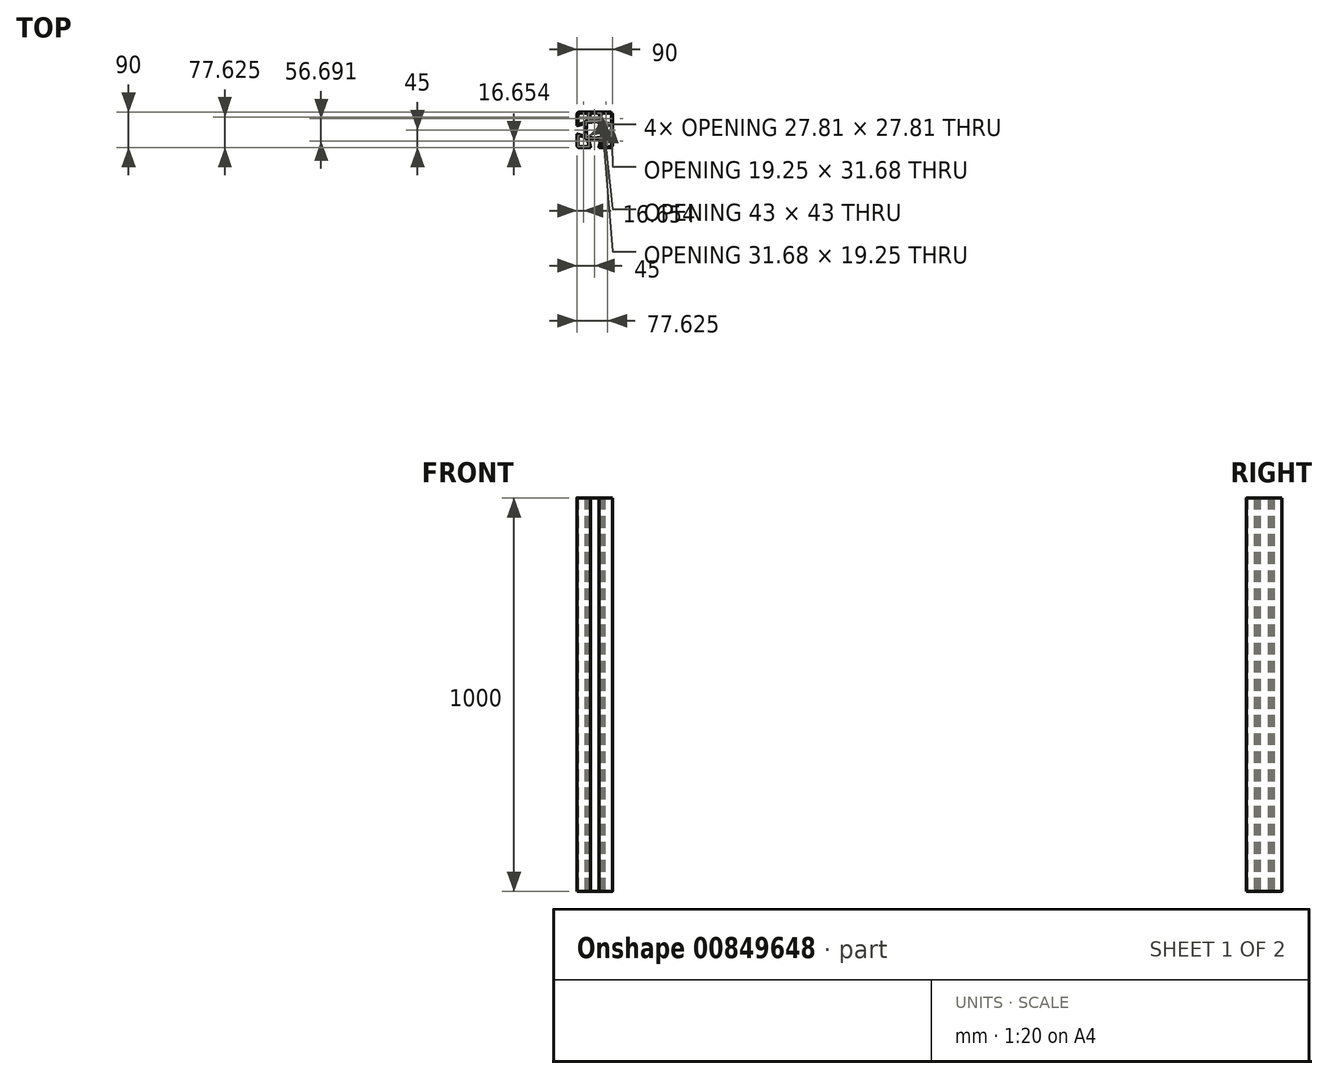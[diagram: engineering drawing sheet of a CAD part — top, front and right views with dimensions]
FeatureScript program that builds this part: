
annotation { "Feature Type Name" : "Feature", "Feature Type Description" : "" }
export const myFeature = defineFeature(function(context is Context, id is Id, definition is map)
    precondition{}
    {
        {
            var Q0;
            Q0=qCreatedBy(makeId("Top.planeOp"),FACE);
            var sketch = newSketch(context, id + "F0", { "sketchPlane" : qUnion([Q0])});
            skLineSegment(sketch, "E0", {"start": v(24.26, -15.8) * mm, "end": v(42.25, -10.99) * mm});
            skLineSegment(sketch, "E1", {"start": v(42.25, -10.99) * mm, "end": v(42.25, 10.99) * mm});
            skLineSegment(sketch, "E2", {"start": v(42.25, 10.99) * mm, "end": v(24.26, 15.8) * mm});
            skLineSegment(sketch, "E3", {"start": v(23, 14.84) * mm, "end": v(23, 9.27) * mm});
            skLineSegment(sketch, "E4", {"start": v(23, -9.27) * mm, "end": v(23, -14.84) * mm});
            skLineSegment(sketch, "E5", {"start": v(24.48, 18.6) * mm, "end": v(39.73, 14.5) * mm});
            skLineSegment(sketch, "E6", {"start": v(42.25, 16.44) * mm, "end": v(42.25, 39) * mm});
            skLineSegment(sketch, "E7", {"start": v(39, 42.25) * mm, "end": v(16.44, 42.25) * mm});
            skLineSegment(sketch, "E8", {"start": v(14.5, 39.73) * mm, "end": v(18.6, 24.48) * mm});
            skLineSegment(sketch, "E9", {"start": v(20.53, 23) * mm, "end": v(21, 23) * mm});
            skLineSegment(sketch, "E10", {"start": v(23, 21) * mm, "end": v(23, 20.53) * mm});
            skLineSegment(sketch, "E11", {"start": v(-18.6, 24.48) * mm, "end": v(-14.5, 39.73) * mm});
            skLineSegment(sketch, "E12", {"start": v(-16.44, 42.25) * mm, "end": v(-39, 42.25) * mm});
            skLineSegment(sketch, "E13", {"start": v(-42.25, 39) * mm, "end": v(-42.25, 16.44) * mm});
            skLineSegment(sketch, "E14", {"start": v(-39.73, 14.5) * mm, "end": v(-24.48, 18.6) * mm});
            skLineSegment(sketch, "E15", {"start": v(-23, 20.53) * mm, "end": v(-23, 21) * mm});
            skLineSegment(sketch, "E16", {"start": v(-21, 23) * mm, "end": v(-20.53, 23) * mm});
            skLineSegment(sketch, "E17", {"start": v(-19.25, -20.25) * mm, "end": v(-7.4, -20.25) * mm});
            skLineSegment(sketch, "E18", {"start": v(7.4, -20.25) * mm, "end": v(19.25, -20.25) * mm});
            skLineSegment(sketch, "E19", {"start": v(20.25, -19.25) * mm, "end": v(20.25, -7.4) * mm});
            skLineSegment(sketch, "E20", {"start": v(20.25, 7.4) * mm, "end": v(20.25, 19.25) * mm});
            skLineSegment(sketch, "E21", {"start": v(19.25, 20.25) * mm, "end": v(7.4, 20.25) * mm});
            skLineSegment(sketch, "E22", {"start": v(-7.4, 20.25) * mm, "end": v(-19.25, 20.25) * mm});
            skLineSegment(sketch, "E23", {"start": v(-20.25, 19.25) * mm, "end": v(-20.25, 7.4) * mm});
            skLineSegment(sketch, "E24", {"start": v(-20.25, -7.4) * mm, "end": v(-20.25, -19.25) * mm});
            skLineSegment(sketch, "E25", {"start": v(9.27, -23) * mm, "end": v(14.84, -23) * mm});
            skLineSegment(sketch, "E26", {"start": v(-14.84, -23) * mm, "end": v(-9.27, -23) * mm});
            skLineSegment(sketch, "E27", {"start": v(-10.67, -43.43) * mm, "end": v(-15.8, -24.26) * mm});
            skLineSegment(sketch, "E28", {"start": v(-39, -45) * mm, "end": v(-11.88, -45) * mm});
            skLineSegment(sketch, "E29", {"start": v(-45, -11.88) * mm, "end": v(-45, -39) * mm});
            skLineSegment(sketch, "E30", {"start": v(-24.26, -15.8) * mm, "end": v(-43.43, -10.67) * mm});
            skLineSegment(sketch, "E31", {"start": v(-23, -9.27) * mm, "end": v(-23, -14.84) * mm});
            skLineSegment(sketch, "E32", {"start": v(-23, 14.84) * mm, "end": v(-23, 9.27) * mm});
            skLineSegment(sketch, "E33", {"start": v(-43.43, 10.67) * mm, "end": v(-24.26, 15.8) * mm});
            skLineSegment(sketch, "E34", {"start": v(-45, 39) * mm, "end": v(-45, 11.88) * mm});
            skLineSegment(sketch, "E35", {"start": v(39, 45) * mm, "end": v(-39, 45) * mm});
            skLineSegment(sketch, "E36", {"start": v(45, -39) * mm, "end": v(45, 39) * mm});
            skLineSegment(sketch, "E37", {"start": v(11.88, -45) * mm, "end": v(39, -45) * mm});
            skLineSegment(sketch, "E38", {"start": v(15.8, -24.26) * mm, "end": v(10.67, -43.43) * mm});
            skLineSegment(sketch, "E39", {"start": v(-14.84, 23) * mm, "end": v(-9.27, 23) * mm});
            skLineSegment(sketch, "E40", {"start": v(9.27, 23) * mm, "end": v(14.84, 23) * mm});
            skLineSegment(sketch, "E41", {"start": v(15.8, 24.26) * mm, "end": v(10.99, 42.25) * mm});
            skLineSegment(sketch, "E42", {"start": v(10.99, 42.25) * mm, "end": v(-10.99, 42.25) * mm});
            skLineSegment(sketch, "E43", {"start": v(-10.99, 42.25) * mm, "end": v(-15.8, 24.26) * mm});
            skLineSegment(sketch, "E44", {"start": v(-24.48, -18.6) * mm, "end": v(-39.73, -14.5) * mm});
            skLineSegment(sketch, "E45", {"start": v(-42.25, -16.44) * mm, "end": v(-42.25, -39) * mm});
            skLineSegment(sketch, "E46", {"start": v(-39, -42.25) * mm, "end": v(-16.44, -42.25) * mm});
            skLineSegment(sketch, "E47", {"start": v(-14.5, -39.73) * mm, "end": v(-18.6, -24.48) * mm});
            skLineSegment(sketch, "E48", {"start": v(-20.53, -23) * mm, "end": v(-21, -23) * mm});
            skLineSegment(sketch, "E49", {"start": v(-23, -21) * mm, "end": v(-23, -20.53) * mm});
            skLineSegment(sketch, "E50", {"start": v(18.6, -24.48) * mm, "end": v(14.5, -39.73) * mm});
            skLineSegment(sketch, "E51", {"start": v(16.44, -42.25) * mm, "end": v(39, -42.25) * mm});
            skLineSegment(sketch, "E52", {"start": v(42.25, -39) * mm, "end": v(42.25, -16.44) * mm});
            skLineSegment(sketch, "E53", {"start": v(39.73, -14.5) * mm, "end": v(24.48, -18.6) * mm});
            skLineSegment(sketch, "E54", {"start": v(23, -20.53) * mm, "end": v(23, -21) * mm});
            skLineSegment(sketch, "E55", {"start": v(21, -23) * mm, "end": v(20.53, -23) * mm});
            skArc(sketch, "E56", {"start": v(23, -14.84) * mm, "mid": v(23.4, -15.64) * mm, "end": v(24.26, -15.8) * mm});
            skArc(sketch, "E57", {"start": v(24.26, 15.8) * mm, "mid": v(23.4, 15.64) * mm, "end": v(23, 14.84) * mm});
            skArc(sketch, "E58", {"start": v(23, 9.27) * mm, "mid": v(23.02, 9.06) * mm, "end": v(23.09, 8.86) * mm});
            skArc(sketch, "E59", {"start": v(23.09, -8.86) * mm, "mid": v(25, 0) * mm, "end": v(23.09, 8.86) * mm});
            skArc(sketch, "E60", {"start": v(23.09, -8.86) * mm, "mid": v(23.02, -9.06) * mm, "end": v(23, -9.27) * mm});
            skArc(sketch, "E61", {"start": v(23, 20.53) * mm, "mid": v(23.41, 19.3) * mm, "end": v(24.48, 18.6) * mm});
            skArc(sketch, "E62", {"start": v(39.73, 14.5) * mm, "mid": v(41.47, 14.85) * mm, "end": v(42.25, 16.44) * mm});
            skArc(sketch, "E63", {"start": v(42.25, 39) * mm, "mid": v(41.3, 41.3) * mm, "end": v(39, 42.25) * mm});
            skArc(sketch, "E64", {"start": v(16.44, 42.25) * mm, "mid": v(14.85, 41.47) * mm, "end": v(14.5, 39.73) * mm});
            skArc(sketch, "E65", {"start": v(18.6, 24.48) * mm, "mid": v(19.3, 23.41) * mm, "end": v(20.53, 23) * mm});
            skArc(sketch, "E66", {"start": v(23, 21) * mm, "mid": v(22.41, 22.41) * mm, "end": v(21, 23) * mm});
            skArc(sketch, "E67", {"start": v(-20.53, 23) * mm, "mid": v(-19.3, 23.41) * mm, "end": v(-18.6, 24.48) * mm});
            skArc(sketch, "E68", {"start": v(-14.5, 39.73) * mm, "mid": v(-14.85, 41.47) * mm, "end": v(-16.44, 42.25) * mm});
            skArc(sketch, "E69", {"start": v(-39, 42.25) * mm, "mid": v(-41.3, 41.3) * mm, "end": v(-42.25, 39) * mm});
            skArc(sketch, "E70", {"start": v(-42.25, 16.44) * mm, "mid": v(-41.47, 14.85) * mm, "end": v(-39.73, 14.5) * mm});
            skArc(sketch, "E71", {"start": v(-24.48, 18.6) * mm, "mid": v(-23.41, 19.3) * mm, "end": v(-23, 20.53) * mm});
            skArc(sketch, "E72", {"start": v(-21, 23) * mm, "mid": v(-22.41, 22.41) * mm, "end": v(-23, 21) * mm});
            skArc(sketch, "E73", {"start": v(-20.25, -19.25) * mm, "mid": v(-19.96, -19.96) * mm, "end": v(-19.25, -20.25) * mm});
            skArc(sketch, "E74", {"start": v(-7.07, -20.3) * mm, "mid": v(-7.23, -20.26) * mm, "end": v(-7.4, -20.25) * mm});
            skArc(sketch, "E75", {"start": v(-7.07, -20.3) * mm, "mid": v(0, -21.5) * mm, "end": v(7.07, -20.3) * mm});
            skArc(sketch, "E76", {"start": v(7.4, -20.25) * mm, "mid": v(7.23, -20.26) * mm, "end": v(7.07, -20.3) * mm});
            skArc(sketch, "E77", {"start": v(19.25, -20.25) * mm, "mid": v(19.96, -19.96) * mm, "end": v(20.25, -19.25) * mm});
            skArc(sketch, "E78", {"start": v(20.3, -7.07) * mm, "mid": v(20.26, -7.23) * mm, "end": v(20.25, -7.4) * mm});
            skArc(sketch, "E79", {"start": v(20.3, -7.07) * mm, "mid": v(21.5, 0) * mm, "end": v(20.3, 7.07) * mm});
            skArc(sketch, "E80", {"start": v(20.25, 7.4) * mm, "mid": v(20.26, 7.23) * mm, "end": v(20.3, 7.07) * mm});
            skArc(sketch, "E81", {"start": v(20.25, 19.25) * mm, "mid": v(19.96, 19.96) * mm, "end": v(19.25, 20.25) * mm});
            skArc(sketch, "E82", {"start": v(7.07, 20.3) * mm, "mid": v(7.23, 20.26) * mm, "end": v(7.4, 20.25) * mm});
            skArc(sketch, "E83", {"start": v(7.07, 20.3) * mm, "mid": v(0, 21.5) * mm, "end": v(-7.07, 20.3) * mm});
            skArc(sketch, "E84", {"start": v(-7.4, 20.25) * mm, "mid": v(-7.23, 20.26) * mm, "end": v(-7.07, 20.3) * mm});
            skArc(sketch, "E85", {"start": v(-19.25, 20.25) * mm, "mid": v(-19.96, 19.96) * mm, "end": v(-20.25, 19.25) * mm});
            skArc(sketch, "E86", {"start": v(-20.3, 7.07) * mm, "mid": v(-20.26, 7.23) * mm, "end": v(-20.25, 7.4) * mm});
            skArc(sketch, "E87", {"start": v(-20.3, 7.07) * mm, "mid": v(-21.5, 0) * mm, "end": v(-20.3, -7.07) * mm});
            skArc(sketch, "E88", {"start": v(-20.25, -7.4) * mm, "mid": v(-20.26, -7.23) * mm, "end": v(-20.3, -7.07) * mm});
            skArc(sketch, "E89", {"start": v(15.8, -24.26) * mm, "mid": v(15.64, -23.4) * mm, "end": v(14.84, -23) * mm});
            skArc(sketch, "E90", {"start": v(9.27, -23) * mm, "mid": v(9.06, -23.02) * mm, "end": v(8.86, -23.09) * mm});
            skArc(sketch, "E91", {"start": v(-8.86, -23.09) * mm, "mid": v(0, -25) * mm, "end": v(8.86, -23.09) * mm});
            skArc(sketch, "E92", {"start": v(-8.86, -23.09) * mm, "mid": v(-9.06, -23.02) * mm, "end": v(-9.27, -23) * mm});
            skArc(sketch, "E93", {"start": v(-14.84, -23) * mm, "mid": v(-15.64, -23.4) * mm, "end": v(-15.8, -24.26) * mm});
            skArc(sketch, "E94", {"start": v(-11.88, -45) * mm, "mid": v(-10.89, -44.51) * mm, "end": v(-10.67, -43.43) * mm});
            skArc(sketch, "E95", {"start": v(-45, -39) * mm, "mid": v(-43.24, -43.24) * mm, "end": v(-39, -45) * mm});
            skArc(sketch, "E96", {"start": v(-43.43, -10.67) * mm, "mid": v(-44.51, -10.89) * mm, "end": v(-45, -11.88) * mm});
            skArc(sketch, "E97", {"start": v(-24.26, -15.8) * mm, "mid": v(-23.4, -15.64) * mm, "end": v(-23, -14.84) * mm});
            skArc(sketch, "E98", {"start": v(-23, -9.27) * mm, "mid": v(-23.02, -9.06) * mm, "end": v(-23.09, -8.86) * mm});
            skArc(sketch, "E99", {"start": v(-23.09, 8.86) * mm, "mid": v(-25, 0) * mm, "end": v(-23.09, -8.86) * mm});
            skArc(sketch, "E100", {"start": v(-23.09, 8.86) * mm, "mid": v(-23.02, 9.06) * mm, "end": v(-23, 9.27) * mm});
            skArc(sketch, "E101", {"start": v(-23, 14.84) * mm, "mid": v(-23.4, 15.64) * mm, "end": v(-24.26, 15.8) * mm});
            skArc(sketch, "E102", {"start": v(-45, 11.88) * mm, "mid": v(-44.51, 10.89) * mm, "end": v(-43.43, 10.67) * mm});
            skArc(sketch, "E103", {"start": v(-39, 45) * mm, "mid": v(-43.24, 43.24) * mm, "end": v(-45, 39) * mm});
            skArc(sketch, "E104", {"start": v(45, 39) * mm, "mid": v(43.24, 43.24) * mm, "end": v(39, 45) * mm});
            skArc(sketch, "E105", {"start": v(39, -45) * mm, "mid": v(43.24, -43.24) * mm, "end": v(45, -39) * mm});
            skArc(sketch, "E106", {"start": v(10.67, -43.43) * mm, "mid": v(10.89, -44.51) * mm, "end": v(11.88, -45) * mm});
            skArc(sketch, "E107", {"start": v(-15.8, 24.26) * mm, "mid": v(-15.64, 23.4) * mm, "end": v(-14.84, 23) * mm});
            skArc(sketch, "E108", {"start": v(-9.27, 23) * mm, "mid": v(-9.06, 23.02) * mm, "end": v(-8.86, 23.09) * mm});
            skArc(sketch, "E109", {"start": v(8.86, 23.09) * mm, "mid": v(0, 25) * mm, "end": v(-8.86, 23.09) * mm});
            skArc(sketch, "E110", {"start": v(8.86, 23.09) * mm, "mid": v(9.06, 23.02) * mm, "end": v(9.27, 23) * mm});
            skArc(sketch, "E111", {"start": v(14.84, 23) * mm, "mid": v(15.64, 23.4) * mm, "end": v(15.8, 24.26) * mm});
            skArc(sketch, "E112", {"start": v(-23, -20.53) * mm, "mid": v(-23.41, -19.3) * mm, "end": v(-24.48, -18.6) * mm});
            skArc(sketch, "E113", {"start": v(-39.73, -14.5) * mm, "mid": v(-41.47, -14.85) * mm, "end": v(-42.25, -16.44) * mm});
            skArc(sketch, "E114", {"start": v(-42.25, -39) * mm, "mid": v(-41.3, -41.3) * mm, "end": v(-39, -42.25) * mm});
            skArc(sketch, "E115", {"start": v(-16.44, -42.25) * mm, "mid": v(-14.85, -41.47) * mm, "end": v(-14.5, -39.73) * mm});
            skArc(sketch, "E116", {"start": v(-18.6, -24.48) * mm, "mid": v(-19.3, -23.41) * mm, "end": v(-20.53, -23) * mm});
            skArc(sketch, "E117", {"start": v(-23, -21) * mm, "mid": v(-22.41, -22.41) * mm, "end": v(-21, -23) * mm});
            skArc(sketch, "E118", {"start": v(20.53, -23) * mm, "mid": v(19.3, -23.41) * mm, "end": v(18.6, -24.48) * mm});
            skArc(sketch, "E119", {"start": v(14.5, -39.73) * mm, "mid": v(14.85, -41.47) * mm, "end": v(16.44, -42.25) * mm});
            skArc(sketch, "E120", {"start": v(39, -42.25) * mm, "mid": v(41.3, -41.3) * mm, "end": v(42.25, -39) * mm});
            skArc(sketch, "E121", {"start": v(42.25, -16.44) * mm, "mid": v(41.47, -14.85) * mm, "end": v(39.73, -14.5) * mm});
            skArc(sketch, "E122", {"start": v(24.48, -18.6) * mm, "mid": v(23.41, -19.3) * mm, "end": v(23, -20.53) * mm});
            skArc(sketch, "E123", {"start": v(21, -23) * mm, "mid": v(22.41, -22.41) * mm, "end": v(23, -21) * mm});
            skLineSegment(sketch, "E124.1.0.0", {"start": v(57.75, 39) * mm, "end": v(57.75, 16.44) * mm});
            skLineSegment(sketch, "E124.1.0.1", {"start": v(115.8, 24.26) * mm, "end": v(110.99, 42.25) * mm});
            skLineSegment(sketch, "E124.1.0.2", {"start": v(89.01, 42.25) * mm, "end": v(84.2, 24.26) * mm});
            skArc(sketch, "E124.1.0.3", {"start": v(107.07, 20.3) * mm, "mid": v(100, 21.5) * mm, "end": v(92.93, 20.3) * mm});
            skLineSegment(sketch, "E124.1.0.4", {"start": v(60.27, 14.5) * mm, "end": v(75.52, 18.6) * mm});
            skLineSegment(sketch, "E124.1.0.5", {"start": v(81.4, 24.48) * mm, "end": v(85.5, 39.73) * mm});
            skLineSegment(sketch, "E124.1.0.6", {"start": v(139, 45) * mm, "end": v(61, 45) * mm});
            skArc(sketch, "E124.1.0.7", {"start": v(139, -45) * mm, "mid": v(143.24, -43.24) * mm, "end": v(145, -39) * mm});
            skArc(sketch, "E124.1.0.8", {"start": v(92.93, -20.3) * mm, "mid": v(100, -21.5) * mm, "end": v(107.07, -20.3) * mm});
            skLineSegment(sketch, "E124.1.0.9", {"start": v(120.25, -19.25) * mm, "end": v(120.25, -7.4) * mm});
            skLineSegment(sketch, "E124.1.0.10", {"start": v(79.75, 19.25) * mm, "end": v(79.75, 7.4) * mm});
            skLineSegment(sketch, "E124.1.0.11", {"start": v(118.6, -24.48) * mm, "end": v(114.5, -39.73) * mm});
            skArc(sketch, "E124.1.0.12", {"start": v(76.91, 8.86) * mm, "mid": v(75, 0) * mm, "end": v(76.91, -8.86) * mm});
            skLineSegment(sketch, "E124.1.0.13", {"start": v(114.5, 39.73) * mm, "end": v(118.6, 24.48) * mm});
            skLineSegment(sketch, "E124.1.0.14", {"start": v(116.44, -42.25) * mm, "end": v(139, -42.25) * mm});
            skLineSegment(sketch, "E124.1.0.15", {"start": v(110.99, 42.25) * mm, "end": v(89.01, 42.25) * mm});
            skLineSegment(sketch, "E124.1.0.16", {"start": v(55, 39) * mm, "end": v(55, 11.88) * mm});
            skLineSegment(sketch, "E124.1.0.17", {"start": v(120.25, 7.4) * mm, "end": v(120.25, 19.25) * mm});
            skLineSegment(sketch, "E124.1.0.18", {"start": v(55, -11.88) * mm, "end": v(55, -39) * mm});
            skLineSegment(sketch, "E124.1.0.19", {"start": v(142.25, -39) * mm, "end": v(142.25, -16.44) * mm});
            skLineSegment(sketch, "E124.1.0.20", {"start": v(57.75, -16.44) * mm, "end": v(57.75, -39) * mm});
            skArc(sketch, "E124.1.0.21", {"start": v(61, 45) * mm, "mid": v(56.76, 43.24) * mm, "end": v(55, 39) * mm});
            skArc(sketch, "E124.1.0.22", {"start": v(123.09, -8.86) * mm, "mid": v(125, 0) * mm, "end": v(123.09, 8.86) * mm});
            skArc(sketch, "E124.1.0.23", {"start": v(108.86, 23.09) * mm, "mid": v(100, 25) * mm, "end": v(91.14, 23.09) * mm});
            skLineSegment(sketch, "E124.1.0.24", {"start": v(142.25, 16.44) * mm, "end": v(142.25, 39) * mm});
            skArc(sketch, "E124.1.0.25", {"start": v(55, -39) * mm, "mid": v(56.76, -43.24) * mm, "end": v(61, -45) * mm});
            skArc(sketch, "E124.1.0.26", {"start": v(120.3, -7.07) * mm, "mid": v(121.5, 0) * mm, "end": v(120.3, 7.07) * mm});
            skLineSegment(sketch, "E124.1.0.27", {"start": v(142.25, -10.99) * mm, "end": v(142.25, 10.99) * mm});
            skLineSegment(sketch, "E124.1.0.28", {"start": v(139.73, -14.5) * mm, "end": v(124.48, -18.6) * mm});
            skLineSegment(sketch, "E124.1.0.29", {"start": v(79.75, -7.4) * mm, "end": v(79.75, -19.25) * mm});
            skLineSegment(sketch, "E124.1.0.30", {"start": v(124.48, 18.6) * mm, "end": v(139.73, 14.5) * mm});
            skLineSegment(sketch, "E124.1.0.31", {"start": v(75.74, -15.8) * mm, "end": v(56.57, -10.67) * mm});
            skLineSegment(sketch, "E124.1.0.32", {"start": v(139, 42.25) * mm, "end": v(116.44, 42.25) * mm});
            skLineSegment(sketch, "E124.1.0.33", {"start": v(124.26, -15.8) * mm, "end": v(142.25, -10.99) * mm});
            skLineSegment(sketch, "E124.1.0.34", {"start": v(89.33, -43.43) * mm, "end": v(84.2, -24.26) * mm});
            skLineSegment(sketch, "E124.1.0.35", {"start": v(75.52, -18.6) * mm, "end": v(60.27, -14.5) * mm});
            skLineSegment(sketch, "E124.1.0.36", {"start": v(61, -42.25) * mm, "end": v(83.56, -42.25) * mm});
            skLineSegment(sketch, "E124.1.0.37", {"start": v(115.8, -24.26) * mm, "end": v(110.67, -43.43) * mm});
            skLineSegment(sketch, "E124.1.0.38", {"start": v(61, -45) * mm, "end": v(88.12, -45) * mm});
            skLineSegment(sketch, "E124.1.0.39", {"start": v(142.25, 10.99) * mm, "end": v(124.26, 15.8) * mm});
            skArc(sketch, "E124.1.0.40", {"start": v(79.7, 7.07) * mm, "mid": v(78.5, 0) * mm, "end": v(79.7, -7.07) * mm});
            skLineSegment(sketch, "E124.1.0.41", {"start": v(85.5, -39.73) * mm, "end": v(81.4, -24.48) * mm});
            skLineSegment(sketch, "E124.1.0.42", {"start": v(56.57, 10.67) * mm, "end": v(75.74, 15.8) * mm});
            skArc(sketch, "E124.1.0.43", {"start": v(145, 39) * mm, "mid": v(143.24, 43.24) * mm, "end": v(139, 45) * mm});
            skArc(sketch, "E124.1.0.44", {"start": v(91.14, -23.09) * mm, "mid": v(100, -25) * mm, "end": v(108.86, -23.09) * mm});
            skLineSegment(sketch, "E124.1.0.45", {"start": v(83.56, 42.25) * mm, "end": v(61, 42.25) * mm});
            skLineSegment(sketch, "E124.1.0.46", {"start": v(111.88, -45) * mm, "end": v(139, -45) * mm});
            skLineSegment(sketch, "E124.1.0.47", {"start": v(145, -39) * mm, "end": v(145, 39) * mm});
            skLineSegment(sketch, "E124.1.0.48", {"start": v(77, 14.84) * mm, "end": v(77, 9.27) * mm});
            skArc(sketch, "E124.1.0.49", {"start": v(57.75, 16.44) * mm, "mid": v(58.53, 14.85) * mm, "end": v(60.27, 14.5) * mm});
            skLineSegment(sketch, "E124.1.0.50", {"start": v(119.25, 20.25) * mm, "end": v(107.4, 20.25) * mm});
            skArc(sketch, "E124.1.0.51", {"start": v(114.84, 23) * mm, "mid": v(115.64, 23.4) * mm, "end": v(115.8, 24.26) * mm});
            skArc(sketch, "E124.1.0.52", {"start": v(84.2, 24.26) * mm, "mid": v(84.36, 23.4) * mm, "end": v(85.16, 23) * mm});
            skArc(sketch, "E124.1.0.53", {"start": v(56.57, -10.67) * mm, "mid": v(55.49, -10.89) * mm, "end": v(55, -11.88) * mm});
            skArc(sketch, "E124.1.0.54", {"start": v(77, 14.84) * mm, "mid": v(76.6, 15.64) * mm, "end": v(75.74, 15.8) * mm});
            skArc(sketch, "E124.1.0.55", {"start": v(85.5, 39.73) * mm, "mid": v(85.15, 41.47) * mm, "end": v(83.56, 42.25) * mm});
            skArc(sketch, "E124.1.0.56", {"start": v(139, -42.25) * mm, "mid": v(141.3, -41.3) * mm, "end": v(142.25, -39) * mm});
            skLineSegment(sketch, "E124.1.0.57", {"start": v(107.4, -20.25) * mm, "end": v(119.25, -20.25) * mm});
            skArc(sketch, "E124.1.0.58", {"start": v(61, 42.25) * mm, "mid": v(58.7, 41.3) * mm, "end": v(57.75, 39) * mm});
            skArc(sketch, "E124.1.0.59", {"start": v(83.56, -42.25) * mm, "mid": v(85.15, -41.47) * mm, "end": v(85.5, -39.73) * mm});
            skLineSegment(sketch, "E124.1.0.60", {"start": v(80.75, -20.25) * mm, "end": v(92.6, -20.25) * mm});
            skArc(sketch, "E124.1.0.61", {"start": v(123, -14.84) * mm, "mid": v(123.4, -15.64) * mm, "end": v(124.26, -15.8) * mm});
            skArc(sketch, "E124.1.0.62", {"start": v(142.25, -16.44) * mm, "mid": v(141.47, -14.85) * mm, "end": v(139.73, -14.5) * mm});
            skLineSegment(sketch, "E124.1.0.63", {"start": v(123, 14.84) * mm, "end": v(123, 9.27) * mm});
            skArc(sketch, "E124.1.0.64", {"start": v(60.27, -14.5) * mm, "mid": v(58.53, -14.85) * mm, "end": v(57.75, -16.44) * mm});
            skArc(sketch, "E124.1.0.65", {"start": v(116.44, 42.25) * mm, "mid": v(114.85, 41.47) * mm, "end": v(114.5, 39.73) * mm});
            skArc(sketch, "E124.1.0.66", {"start": v(110.67, -43.43) * mm, "mid": v(110.89, -44.51) * mm, "end": v(111.88, -45) * mm});
            skArc(sketch, "E124.1.0.67", {"start": v(118.6, 24.48) * mm, "mid": v(119.3, 23.41) * mm, "end": v(120.53, 23) * mm});
            skLineSegment(sketch, "E124.1.0.68", {"start": v(77, -9.27) * mm, "end": v(77, -14.84) * mm});
            skArc(sketch, "E124.1.0.69", {"start": v(75.74, -15.8) * mm, "mid": v(76.6, -15.64) * mm, "end": v(77, -14.84) * mm});
            skLineSegment(sketch, "E124.1.0.70", {"start": v(123, -9.27) * mm, "end": v(123, -14.84) * mm});
            skLineSegment(sketch, "E124.1.0.71", {"start": v(109.27, 23) * mm, "end": v(114.84, 23) * mm});
            skArc(sketch, "E124.1.0.72", {"start": v(55, 11.88) * mm, "mid": v(55.49, 10.89) * mm, "end": v(56.57, 10.67) * mm});
            skArc(sketch, "E124.1.0.73", {"start": v(139.73, 14.5) * mm, "mid": v(141.47, 14.85) * mm, "end": v(142.25, 16.44) * mm});
            skLineSegment(sketch, "E124.1.0.74", {"start": v(92.6, 20.25) * mm, "end": v(80.75, 20.25) * mm});
            skArc(sketch, "E124.1.0.75", {"start": v(114.5, -39.73) * mm, "mid": v(114.85, -41.47) * mm, "end": v(116.44, -42.25) * mm});
            skLineSegment(sketch, "E124.1.0.76", {"start": v(109.27, -23) * mm, "end": v(114.84, -23) * mm});
            skLineSegment(sketch, "E124.1.0.77", {"start": v(85.16, 23) * mm, "end": v(90.73, 23) * mm});
            skArc(sketch, "E124.1.0.78", {"start": v(120.25, 19.25) * mm, "mid": v(119.96, 19.96) * mm, "end": v(119.25, 20.25) * mm});
            skArc(sketch, "E124.1.0.79", {"start": v(142.25, 39) * mm, "mid": v(141.3, 41.3) * mm, "end": v(139, 42.25) * mm});
            skArc(sketch, "E124.1.0.80", {"start": v(120.53, -23) * mm, "mid": v(119.3, -23.41) * mm, "end": v(118.6, -24.48) * mm});
            skArc(sketch, "E124.1.0.81", {"start": v(79.47, 23) * mm, "mid": v(80.7, 23.41) * mm, "end": v(81.4, 24.48) * mm});
            skArc(sketch, "E124.1.0.82", {"start": v(115.8, -24.26) * mm, "mid": v(115.64, -23.4) * mm, "end": v(114.84, -23) * mm});
            skArc(sketch, "E124.1.0.83", {"start": v(85.16, -23) * mm, "mid": v(84.36, -23.4) * mm, "end": v(84.2, -24.26) * mm});
            skArc(sketch, "E124.1.0.84", {"start": v(119.25, -20.25) * mm, "mid": v(119.96, -19.96) * mm, "end": v(120.25, -19.25) * mm});
            skArc(sketch, "E124.1.0.85", {"start": v(79.75, -19.25) * mm, "mid": v(80.04, -19.96) * mm, "end": v(80.75, -20.25) * mm});
            skArc(sketch, "E124.1.0.86", {"start": v(80.75, 20.25) * mm, "mid": v(80.04, 19.96) * mm, "end": v(79.75, 19.25) * mm});
            skArc(sketch, "E124.1.0.87", {"start": v(88.12, -45) * mm, "mid": v(89.11, -44.51) * mm, "end": v(89.33, -43.43) * mm});
            skLineSegment(sketch, "E124.1.0.88", {"start": v(85.16, -23) * mm, "end": v(90.73, -23) * mm});
            skArc(sketch, "E124.1.0.89", {"start": v(81.4, -24.48) * mm, "mid": v(80.7, -23.41) * mm, "end": v(79.47, -23) * mm});
            skArc(sketch, "E124.1.0.90", {"start": v(57.75, -39) * mm, "mid": v(58.7, -41.3) * mm, "end": v(61, -42.25) * mm});
            skArc(sketch, "E124.1.0.91", {"start": v(124.26, 15.8) * mm, "mid": v(123.4, 15.64) * mm, "end": v(123, 14.84) * mm});
            skArc(sketch, "E124.1.0.92", {"start": v(123.09, -8.86) * mm, "mid": v(123.02, -9.06) * mm, "end": v(123, -9.27) * mm});
            skArc(sketch, "E124.1.0.93", {"start": v(77, -20.53) * mm, "mid": v(76.59, -19.3) * mm, "end": v(75.52, -18.6) * mm});
            skArc(sketch, "E124.1.0.94", {"start": v(77, -21) * mm, "mid": v(77.59, -22.41) * mm, "end": v(79, -23) * mm});
            skLineSegment(sketch, "E124.1.0.95", {"start": v(79, 23) * mm, "end": v(79.47, 23) * mm});
            skArc(sketch, "E124.1.0.96", {"start": v(108.86, 23.09) * mm, "mid": v(109.06, 23.02) * mm, "end": v(109.27, 23) * mm});
            skArc(sketch, "E124.1.0.97", {"start": v(123, 9.27) * mm, "mid": v(123.02, 9.06) * mm, "end": v(123.09, 8.86) * mm});
            skArc(sketch, "E124.1.0.98", {"start": v(120.25, 7.4) * mm, "mid": v(120.26, 7.23) * mm, "end": v(120.3, 7.07) * mm});
            skArc(sketch, "E124.1.0.99", {"start": v(79, 23) * mm, "mid": v(77.59, 22.41) * mm, "end": v(77, 21) * mm});
            skArc(sketch, "E124.1.0.100", {"start": v(79.75, -7.4) * mm, "mid": v(79.74, -7.23) * mm, "end": v(79.7, -7.07) * mm});
            skArc(sketch, "E124.1.0.101", {"start": v(76.91, 8.86) * mm, "mid": v(76.98, 9.06) * mm, "end": v(77, 9.27) * mm});
            skArc(sketch, "E124.1.0.102", {"start": v(92.6, 20.25) * mm, "mid": v(92.77, 20.26) * mm, "end": v(92.93, 20.3) * mm});
            skLineSegment(sketch, "E124.1.0.103", {"start": v(79.47, -23) * mm, "end": v(79, -23) * mm});
            skArc(sketch, "E124.1.0.104", {"start": v(120.3, -7.07) * mm, "mid": v(120.26, -7.23) * mm, "end": v(120.25, -7.4) * mm});
            skArc(sketch, "E124.1.0.105", {"start": v(79.7, 7.07) * mm, "mid": v(79.74, 7.23) * mm, "end": v(79.75, 7.4) * mm});
            skArc(sketch, "E124.1.0.106", {"start": v(90.73, 23) * mm, "mid": v(90.94, 23.02) * mm, "end": v(91.14, 23.09) * mm});
            skLineSegment(sketch, "E124.1.0.107", {"start": v(77, -21) * mm, "end": v(77, -20.53) * mm});
            skArc(sketch, "E124.1.0.108", {"start": v(75.52, 18.6) * mm, "mid": v(76.59, 19.3) * mm, "end": v(77, 20.53) * mm});
            skArc(sketch, "E124.1.0.109", {"start": v(77, -9.27) * mm, "mid": v(76.98, -9.06) * mm, "end": v(76.91, -8.86) * mm});
            skArc(sketch, "E124.1.0.110", {"start": v(107.07, 20.3) * mm, "mid": v(107.23, 20.26) * mm, "end": v(107.4, 20.25) * mm});
            skLineSegment(sketch, "E124.1.0.111", {"start": v(120.53, 23) * mm, "end": v(121, 23) * mm});
            skArc(sketch, "E124.1.0.112", {"start": v(124.48, -18.6) * mm, "mid": v(123.41, -19.3) * mm, "end": v(123, -20.53) * mm});
            skArc(sketch, "E124.1.0.113", {"start": v(107.4, -20.25) * mm, "mid": v(107.23, -20.26) * mm, "end": v(107.07, -20.3) * mm});
            skArc(sketch, "E124.1.0.114", {"start": v(121, -23) * mm, "mid": v(122.41, -22.41) * mm, "end": v(123, -21) * mm});
            skLineSegment(sketch, "E124.1.0.115", {"start": v(121, -23) * mm, "end": v(120.53, -23) * mm});
            skLineSegment(sketch, "E124.1.0.116", {"start": v(123, -20.53) * mm, "end": v(123, -21) * mm});
            skArc(sketch, "E124.1.0.117", {"start": v(109.27, -23) * mm, "mid": v(109.06, -23.02) * mm, "end": v(108.86, -23.09) * mm});
            skArc(sketch, "E124.1.0.118", {"start": v(91.14, -23.09) * mm, "mid": v(90.94, -23.02) * mm, "end": v(90.73, -23) * mm});
            skArc(sketch, "E124.1.0.119", {"start": v(123, 20.53) * mm, "mid": v(123.41, 19.3) * mm, "end": v(124.48, 18.6) * mm});
            skArc(sketch, "E124.1.0.120", {"start": v(92.93, -20.3) * mm, "mid": v(92.77, -20.26) * mm, "end": v(92.6, -20.25) * mm});
            skLineSegment(sketch, "E124.1.0.121", {"start": v(77, 20.53) * mm, "end": v(77, 21) * mm});
            skArc(sketch, "E124.1.0.122", {"start": v(123, 21) * mm, "mid": v(122.41, 22.41) * mm, "end": v(121, 23) * mm});
            skLineSegment(sketch, "E124.1.0.123", {"start": v(123, 21) * mm, "end": v(123, 20.53) * mm});
            skLineSegment(sketch, "E124.2.0.0", {"start": v(157.75, 39) * mm, "end": v(157.75, 16.44) * mm});
            skLineSegment(sketch, "E124.2.0.1", {"start": v(215.8, 24.26) * mm, "end": v(210.99, 42.25) * mm});
            skLineSegment(sketch, "E124.2.0.2", {"start": v(189.01, 42.25) * mm, "end": v(184.2, 24.26) * mm});
            skArc(sketch, "E124.2.0.3", {"start": v(207.07, 20.3) * mm, "mid": v(200, 21.5) * mm, "end": v(192.93, 20.3) * mm});
            skLineSegment(sketch, "E124.2.0.4", {"start": v(160.27, 14.5) * mm, "end": v(175.52, 18.6) * mm});
            skLineSegment(sketch, "E124.2.0.5", {"start": v(181.4, 24.48) * mm, "end": v(185.5, 39.73) * mm});
            skLineSegment(sketch, "E124.2.0.6", {"start": v(239, 45) * mm, "end": v(161, 45) * mm});
            skArc(sketch, "E124.2.0.7", {"start": v(239, -45) * mm, "mid": v(243.24, -43.24) * mm, "end": v(245, -39) * mm});
            skArc(sketch, "E124.2.0.8", {"start": v(192.93, -20.3) * mm, "mid": v(200, -21.5) * mm, "end": v(207.07, -20.3) * mm});
            skLineSegment(sketch, "E124.2.0.9", {"start": v(220.25, -19.25) * mm, "end": v(220.25, -7.4) * mm});
            skLineSegment(sketch, "E124.2.0.10", {"start": v(179.75, 19.25) * mm, "end": v(179.75, 7.4) * mm});
            skLineSegment(sketch, "E124.2.0.11", {"start": v(218.6, -24.48) * mm, "end": v(214.5, -39.73) * mm});
            skArc(sketch, "E124.2.0.12", {"start": v(176.91, 8.86) * mm, "mid": v(175, 0) * mm, "end": v(176.91, -8.86) * mm});
            skLineSegment(sketch, "E124.2.0.13", {"start": v(214.5, 39.73) * mm, "end": v(218.6, 24.48) * mm});
            skLineSegment(sketch, "E124.2.0.14", {"start": v(216.44, -42.25) * mm, "end": v(239, -42.25) * mm});
            skLineSegment(sketch, "E124.2.0.15", {"start": v(210.99, 42.25) * mm, "end": v(189.01, 42.25) * mm});
            skLineSegment(sketch, "E124.2.0.16", {"start": v(155, 39) * mm, "end": v(155, 11.88) * mm});
            skLineSegment(sketch, "E124.2.0.17", {"start": v(220.25, 7.4) * mm, "end": v(220.25, 19.25) * mm});
            skLineSegment(sketch, "E124.2.0.18", {"start": v(155, -11.88) * mm, "end": v(155, -39) * mm});
            skLineSegment(sketch, "E124.2.0.19", {"start": v(242.25, -39) * mm, "end": v(242.25, -16.44) * mm});
            skLineSegment(sketch, "E124.2.0.20", {"start": v(157.75, -16.44) * mm, "end": v(157.75, -39) * mm});
            skArc(sketch, "E124.2.0.21", {"start": v(161, 45) * mm, "mid": v(156.76, 43.24) * mm, "end": v(155, 39) * mm});
            skArc(sketch, "E124.2.0.22", {"start": v(223.09, -8.86) * mm, "mid": v(225, 0) * mm, "end": v(223.09, 8.86) * mm});
            skArc(sketch, "E124.2.0.23", {"start": v(208.86, 23.09) * mm, "mid": v(200, 25) * mm, "end": v(191.14, 23.09) * mm});
            skLineSegment(sketch, "E124.2.0.24", {"start": v(242.25, 16.44) * mm, "end": v(242.25, 39) * mm});
            skArc(sketch, "E124.2.0.25", {"start": v(155, -39) * mm, "mid": v(156.76, -43.24) * mm, "end": v(161, -45) * mm});
            skArc(sketch, "E124.2.0.26", {"start": v(220.3, -7.07) * mm, "mid": v(221.5, 0) * mm, "end": v(220.3, 7.07) * mm});
            skLineSegment(sketch, "E124.2.0.27", {"start": v(242.25, -10.99) * mm, "end": v(242.25, 10.99) * mm});
            skLineSegment(sketch, "E124.2.0.28", {"start": v(239.73, -14.5) * mm, "end": v(224.48, -18.6) * mm});
            skLineSegment(sketch, "E124.2.0.29", {"start": v(179.75, -7.4) * mm, "end": v(179.75, -19.25) * mm});
            skLineSegment(sketch, "E124.2.0.30", {"start": v(224.48, 18.6) * mm, "end": v(239.73, 14.5) * mm});
            skLineSegment(sketch, "E124.2.0.31", {"start": v(175.74, -15.8) * mm, "end": v(156.57, -10.67) * mm});
            skLineSegment(sketch, "E124.2.0.32", {"start": v(239, 42.25) * mm, "end": v(216.44, 42.25) * mm});
            skLineSegment(sketch, "E124.2.0.33", {"start": v(224.26, -15.8) * mm, "end": v(242.25, -10.99) * mm});
            skLineSegment(sketch, "E124.2.0.34", {"start": v(189.33, -43.43) * mm, "end": v(184.2, -24.26) * mm});
            skLineSegment(sketch, "E124.2.0.35", {"start": v(175.52, -18.6) * mm, "end": v(160.27, -14.5) * mm});
            skLineSegment(sketch, "E124.2.0.36", {"start": v(161, -42.25) * mm, "end": v(183.56, -42.25) * mm});
            skLineSegment(sketch, "E124.2.0.37", {"start": v(215.8, -24.26) * mm, "end": v(210.67, -43.43) * mm});
            skLineSegment(sketch, "E124.2.0.38", {"start": v(161, -45) * mm, "end": v(188.12, -45) * mm});
            skLineSegment(sketch, "E124.2.0.39", {"start": v(242.25, 10.99) * mm, "end": v(224.26, 15.8) * mm});
            skArc(sketch, "E124.2.0.40", {"start": v(179.7, 7.07) * mm, "mid": v(178.5, 0) * mm, "end": v(179.7, -7.07) * mm});
            skLineSegment(sketch, "E124.2.0.41", {"start": v(185.5, -39.73) * mm, "end": v(181.4, -24.48) * mm});
            skLineSegment(sketch, "E124.2.0.42", {"start": v(156.57, 10.67) * mm, "end": v(175.74, 15.8) * mm});
            skArc(sketch, "E124.2.0.43", {"start": v(245, 39) * mm, "mid": v(243.24, 43.24) * mm, "end": v(239, 45) * mm});
            skArc(sketch, "E124.2.0.44", {"start": v(191.14, -23.09) * mm, "mid": v(200, -25) * mm, "end": v(208.86, -23.09) * mm});
            skLineSegment(sketch, "E124.2.0.45", {"start": v(183.56, 42.25) * mm, "end": v(161, 42.25) * mm});
            skLineSegment(sketch, "E124.2.0.46", {"start": v(211.88, -45) * mm, "end": v(239, -45) * mm});
            skLineSegment(sketch, "E124.2.0.47", {"start": v(245, -39) * mm, "end": v(245, 39) * mm});
            skLineSegment(sketch, "E124.2.0.48", {"start": v(177, 14.84) * mm, "end": v(177, 9.27) * mm});
            skArc(sketch, "E124.2.0.49", {"start": v(157.75, 16.44) * mm, "mid": v(158.53, 14.85) * mm, "end": v(160.27, 14.5) * mm});
            skLineSegment(sketch, "E124.2.0.50", {"start": v(219.25, 20.25) * mm, "end": v(207.4, 20.25) * mm});
            skArc(sketch, "E124.2.0.51", {"start": v(214.84, 23) * mm, "mid": v(215.64, 23.4) * mm, "end": v(215.8, 24.26) * mm});
            skArc(sketch, "E124.2.0.52", {"start": v(184.2, 24.26) * mm, "mid": v(184.36, 23.4) * mm, "end": v(185.16, 23) * mm});
            skArc(sketch, "E124.2.0.53", {"start": v(156.57, -10.67) * mm, "mid": v(155.49, -10.89) * mm, "end": v(155, -11.88) * mm});
            skArc(sketch, "E124.2.0.54", {"start": v(177, 14.84) * mm, "mid": v(176.6, 15.64) * mm, "end": v(175.74, 15.8) * mm});
            skArc(sketch, "E124.2.0.55", {"start": v(185.5, 39.73) * mm, "mid": v(185.15, 41.47) * mm, "end": v(183.56, 42.25) * mm});
            skArc(sketch, "E124.2.0.56", {"start": v(239, -42.25) * mm, "mid": v(241.3, -41.3) * mm, "end": v(242.25, -39) * mm});
            skLineSegment(sketch, "E124.2.0.57", {"start": v(207.4, -20.25) * mm, "end": v(219.25, -20.25) * mm});
            skArc(sketch, "E124.2.0.58", {"start": v(161, 42.25) * mm, "mid": v(158.7, 41.3) * mm, "end": v(157.75, 39) * mm});
            skArc(sketch, "E124.2.0.59", {"start": v(183.56, -42.25) * mm, "mid": v(185.15, -41.47) * mm, "end": v(185.5, -39.73) * mm});
            skLineSegment(sketch, "E124.2.0.60", {"start": v(180.75, -20.25) * mm, "end": v(192.6, -20.25) * mm});
            skArc(sketch, "E124.2.0.61", {"start": v(223, -14.84) * mm, "mid": v(223.4, -15.64) * mm, "end": v(224.26, -15.8) * mm});
            skArc(sketch, "E124.2.0.62", {"start": v(242.25, -16.44) * mm, "mid": v(241.47, -14.85) * mm, "end": v(239.73, -14.5) * mm});
            skLineSegment(sketch, "E124.2.0.63", {"start": v(223, 14.84) * mm, "end": v(223, 9.27) * mm});
            skArc(sketch, "E124.2.0.64", {"start": v(160.27, -14.5) * mm, "mid": v(158.53, -14.85) * mm, "end": v(157.75, -16.44) * mm});
            skArc(sketch, "E124.2.0.65", {"start": v(216.44, 42.25) * mm, "mid": v(214.85, 41.47) * mm, "end": v(214.5, 39.73) * mm});
            skArc(sketch, "E124.2.0.66", {"start": v(210.67, -43.43) * mm, "mid": v(210.89, -44.51) * mm, "end": v(211.88, -45) * mm});
            skArc(sketch, "E124.2.0.67", {"start": v(218.6, 24.48) * mm, "mid": v(219.3, 23.41) * mm, "end": v(220.53, 23) * mm});
            skLineSegment(sketch, "E124.2.0.68", {"start": v(177, -9.27) * mm, "end": v(177, -14.84) * mm});
            skArc(sketch, "E124.2.0.69", {"start": v(175.74, -15.8) * mm, "mid": v(176.6, -15.64) * mm, "end": v(177, -14.84) * mm});
            skLineSegment(sketch, "E124.2.0.70", {"start": v(223, -9.27) * mm, "end": v(223, -14.84) * mm});
            skLineSegment(sketch, "E124.2.0.71", {"start": v(209.27, 23) * mm, "end": v(214.84, 23) * mm});
            skArc(sketch, "E124.2.0.72", {"start": v(155, 11.88) * mm, "mid": v(155.49, 10.89) * mm, "end": v(156.57, 10.67) * mm});
            skArc(sketch, "E124.2.0.73", {"start": v(239.73, 14.5) * mm, "mid": v(241.47, 14.85) * mm, "end": v(242.25, 16.44) * mm});
            skLineSegment(sketch, "E124.2.0.74", {"start": v(192.6, 20.25) * mm, "end": v(180.75, 20.25) * mm});
            skArc(sketch, "E124.2.0.75", {"start": v(214.5, -39.73) * mm, "mid": v(214.85, -41.47) * mm, "end": v(216.44, -42.25) * mm});
            skLineSegment(sketch, "E124.2.0.76", {"start": v(209.27, -23) * mm, "end": v(214.84, -23) * mm});
            skLineSegment(sketch, "E124.2.0.77", {"start": v(185.16, 23) * mm, "end": v(190.73, 23) * mm});
            skArc(sketch, "E124.2.0.78", {"start": v(220.25, 19.25) * mm, "mid": v(219.96, 19.96) * mm, "end": v(219.25, 20.25) * mm});
            skArc(sketch, "E124.2.0.79", {"start": v(242.25, 39) * mm, "mid": v(241.3, 41.3) * mm, "end": v(239, 42.25) * mm});
            skArc(sketch, "E124.2.0.80", {"start": v(220.53, -23) * mm, "mid": v(219.3, -23.41) * mm, "end": v(218.6, -24.48) * mm});
            skArc(sketch, "E124.2.0.81", {"start": v(179.47, 23) * mm, "mid": v(180.7, 23.41) * mm, "end": v(181.4, 24.48) * mm});
            skArc(sketch, "E124.2.0.82", {"start": v(215.8, -24.26) * mm, "mid": v(215.64, -23.4) * mm, "end": v(214.84, -23) * mm});
            skArc(sketch, "E124.2.0.83", {"start": v(185.16, -23) * mm, "mid": v(184.36, -23.4) * mm, "end": v(184.2, -24.26) * mm});
            skArc(sketch, "E124.2.0.84", {"start": v(219.25, -20.25) * mm, "mid": v(219.96, -19.96) * mm, "end": v(220.25, -19.25) * mm});
            skArc(sketch, "E124.2.0.85", {"start": v(179.75, -19.25) * mm, "mid": v(180.04, -19.96) * mm, "end": v(180.75, -20.25) * mm});
            skArc(sketch, "E124.2.0.86", {"start": v(180.75, 20.25) * mm, "mid": v(180.04, 19.96) * mm, "end": v(179.75, 19.25) * mm});
            skArc(sketch, "E124.2.0.87", {"start": v(188.12, -45) * mm, "mid": v(189.11, -44.51) * mm, "end": v(189.33, -43.43) * mm});
            skLineSegment(sketch, "E124.2.0.88", {"start": v(185.16, -23) * mm, "end": v(190.73, -23) * mm});
            skArc(sketch, "E124.2.0.89", {"start": v(181.4, -24.48) * mm, "mid": v(180.7, -23.41) * mm, "end": v(179.47, -23) * mm});
            skArc(sketch, "E124.2.0.90", {"start": v(157.75, -39) * mm, "mid": v(158.7, -41.3) * mm, "end": v(161, -42.25) * mm});
            skArc(sketch, "E124.2.0.91", {"start": v(224.26, 15.8) * mm, "mid": v(223.4, 15.64) * mm, "end": v(223, 14.84) * mm});
            skArc(sketch, "E124.2.0.92", {"start": v(223.09, -8.86) * mm, "mid": v(223.02, -9.06) * mm, "end": v(223, -9.27) * mm});
            skArc(sketch, "E124.2.0.93", {"start": v(177, -20.53) * mm, "mid": v(176.59, -19.3) * mm, "end": v(175.52, -18.6) * mm});
            skArc(sketch, "E124.2.0.94", {"start": v(177, -21) * mm, "mid": v(177.59, -22.41) * mm, "end": v(179, -23) * mm});
            skLineSegment(sketch, "E124.2.0.95", {"start": v(179, 23) * mm, "end": v(179.47, 23) * mm});
            skArc(sketch, "E124.2.0.96", {"start": v(208.86, 23.09) * mm, "mid": v(209.06, 23.02) * mm, "end": v(209.27, 23) * mm});
            skArc(sketch, "E124.2.0.97", {"start": v(223, 9.27) * mm, "mid": v(223.02, 9.06) * mm, "end": v(223.09, 8.86) * mm});
            skArc(sketch, "E124.2.0.98", {"start": v(220.25, 7.4) * mm, "mid": v(220.26, 7.23) * mm, "end": v(220.3, 7.07) * mm});
            skArc(sketch, "E124.2.0.99", {"start": v(179, 23) * mm, "mid": v(177.59, 22.41) * mm, "end": v(177, 21) * mm});
            skArc(sketch, "E124.2.0.100", {"start": v(179.75, -7.4) * mm, "mid": v(179.74, -7.23) * mm, "end": v(179.7, -7.07) * mm});
            skArc(sketch, "E124.2.0.101", {"start": v(176.91, 8.86) * mm, "mid": v(176.98, 9.06) * mm, "end": v(177, 9.27) * mm});
            skArc(sketch, "E124.2.0.102", {"start": v(192.6, 20.25) * mm, "mid": v(192.77, 20.26) * mm, "end": v(192.93, 20.3) * mm});
            skLineSegment(sketch, "E124.2.0.103", {"start": v(179.47, -23) * mm, "end": v(179, -23) * mm});
            skArc(sketch, "E124.2.0.104", {"start": v(220.3, -7.07) * mm, "mid": v(220.26, -7.23) * mm, "end": v(220.25, -7.4) * mm});
            skArc(sketch, "E124.2.0.105", {"start": v(179.7, 7.07) * mm, "mid": v(179.74, 7.23) * mm, "end": v(179.75, 7.4) * mm});
            skArc(sketch, "E124.2.0.106", {"start": v(190.73, 23) * mm, "mid": v(190.94, 23.02) * mm, "end": v(191.14, 23.09) * mm});
            skLineSegment(sketch, "E124.2.0.107", {"start": v(177, -21) * mm, "end": v(177, -20.53) * mm});
            skArc(sketch, "E124.2.0.108", {"start": v(175.52, 18.6) * mm, "mid": v(176.59, 19.3) * mm, "end": v(177, 20.53) * mm});
            skArc(sketch, "E124.2.0.109", {"start": v(177, -9.27) * mm, "mid": v(176.98, -9.06) * mm, "end": v(176.91, -8.86) * mm});
            skArc(sketch, "E124.2.0.110", {"start": v(207.07, 20.3) * mm, "mid": v(207.23, 20.26) * mm, "end": v(207.4, 20.25) * mm});
            skLineSegment(sketch, "E124.2.0.111", {"start": v(220.53, 23) * mm, "end": v(221, 23) * mm});
            skArc(sketch, "E124.2.0.112", {"start": v(224.48, -18.6) * mm, "mid": v(223.41, -19.3) * mm, "end": v(223, -20.53) * mm});
            skArc(sketch, "E124.2.0.113", {"start": v(207.4, -20.25) * mm, "mid": v(207.23, -20.26) * mm, "end": v(207.07, -20.3) * mm});
            skArc(sketch, "E124.2.0.114", {"start": v(221, -23) * mm, "mid": v(222.41, -22.41) * mm, "end": v(223, -21) * mm});
            skLineSegment(sketch, "E124.2.0.115", {"start": v(221, -23) * mm, "end": v(220.53, -23) * mm});
            skLineSegment(sketch, "E124.2.0.116", {"start": v(223, -20.53) * mm, "end": v(223, -21) * mm});
            skArc(sketch, "E124.2.0.117", {"start": v(209.27, -23) * mm, "mid": v(209.06, -23.02) * mm, "end": v(208.86, -23.09) * mm});
            skArc(sketch, "E124.2.0.118", {"start": v(191.14, -23.09) * mm, "mid": v(190.94, -23.02) * mm, "end": v(190.73, -23) * mm});
            skArc(sketch, "E124.2.0.119", {"start": v(223, 20.53) * mm, "mid": v(223.41, 19.3) * mm, "end": v(224.48, 18.6) * mm});
            skArc(sketch, "E124.2.0.120", {"start": v(192.93, -20.3) * mm, "mid": v(192.77, -20.26) * mm, "end": v(192.6, -20.25) * mm});
            skLineSegment(sketch, "E124.2.0.121", {"start": v(177, 20.53) * mm, "end": v(177, 21) * mm});
            skArc(sketch, "E124.2.0.122", {"start": v(223, 21) * mm, "mid": v(222.41, 22.41) * mm, "end": v(221, 23) * mm});
            skLineSegment(sketch, "E124.2.0.123", {"start": v(223, 21) * mm, "end": v(223, 20.53) * mm});
            skLineSegment(sketch, "E124.3.0.0", {"start": v(257.75, 39) * mm, "end": v(257.75, 16.44) * mm});
            skLineSegment(sketch, "E124.3.0.1", {"start": v(315.8, 24.26) * mm, "end": v(310.99, 42.25) * mm});
            skLineSegment(sketch, "E124.3.0.2", {"start": v(289.01, 42.25) * mm, "end": v(284.2, 24.26) * mm});
            skArc(sketch, "E124.3.0.3", {"start": v(307.07, 20.3) * mm, "mid": v(300, 21.5) * mm, "end": v(292.93, 20.3) * mm});
            skLineSegment(sketch, "E124.3.0.4", {"start": v(260.27, 14.5) * mm, "end": v(275.52, 18.6) * mm});
            skLineSegment(sketch, "E124.3.0.5", {"start": v(281.4, 24.48) * mm, "end": v(285.5, 39.73) * mm});
            skLineSegment(sketch, "E124.3.0.6", {"start": v(339, 45) * mm, "end": v(261, 45) * mm});
            skArc(sketch, "E124.3.0.7", {"start": v(339, -45) * mm, "mid": v(343.24, -43.24) * mm, "end": v(345, -39) * mm});
            skArc(sketch, "E124.3.0.8", {"start": v(292.93, -20.3) * mm, "mid": v(300, -21.5) * mm, "end": v(307.07, -20.3) * mm});
            skLineSegment(sketch, "E124.3.0.9", {"start": v(320.25, -19.25) * mm, "end": v(320.25, -7.4) * mm});
            skLineSegment(sketch, "E124.3.0.10", {"start": v(279.75, 19.25) * mm, "end": v(279.75, 7.4) * mm});
            skLineSegment(sketch, "E124.3.0.11", {"start": v(318.6, -24.48) * mm, "end": v(314.5, -39.73) * mm});
            skArc(sketch, "E124.3.0.12", {"start": v(276.91, 8.86) * mm, "mid": v(275, 0) * mm, "end": v(276.91, -8.86) * mm});
            skLineSegment(sketch, "E124.3.0.13", {"start": v(314.5, 39.73) * mm, "end": v(318.6, 24.48) * mm});
            skLineSegment(sketch, "E124.3.0.14", {"start": v(316.44, -42.25) * mm, "end": v(339, -42.25) * mm});
            skLineSegment(sketch, "E124.3.0.15", {"start": v(310.99, 42.25) * mm, "end": v(289.01, 42.25) * mm});
            skLineSegment(sketch, "E124.3.0.16", {"start": v(255, 39) * mm, "end": v(255, 11.88) * mm});
            skLineSegment(sketch, "E124.3.0.17", {"start": v(320.25, 7.4) * mm, "end": v(320.25, 19.25) * mm});
            skLineSegment(sketch, "E124.3.0.18", {"start": v(255, -11.88) * mm, "end": v(255, -39) * mm});
            skLineSegment(sketch, "E124.3.0.19", {"start": v(342.25, -39) * mm, "end": v(342.25, -16.44) * mm});
            skLineSegment(sketch, "E124.3.0.20", {"start": v(257.75, -16.44) * mm, "end": v(257.75, -39) * mm});
            skArc(sketch, "E124.3.0.21", {"start": v(261, 45) * mm, "mid": v(256.76, 43.24) * mm, "end": v(255, 39) * mm});
            skArc(sketch, "E124.3.0.22", {"start": v(323.09, -8.86) * mm, "mid": v(325, 0) * mm, "end": v(323.09, 8.86) * mm});
            skArc(sketch, "E124.3.0.23", {"start": v(308.86, 23.09) * mm, "mid": v(300, 25) * mm, "end": v(291.14, 23.09) * mm});
            skLineSegment(sketch, "E124.3.0.24", {"start": v(342.25, 16.44) * mm, "end": v(342.25, 39) * mm});
            skArc(sketch, "E124.3.0.25", {"start": v(255, -39) * mm, "mid": v(256.76, -43.24) * mm, "end": v(261, -45) * mm});
            skArc(sketch, "E124.3.0.26", {"start": v(320.3, -7.07) * mm, "mid": v(321.5, 0) * mm, "end": v(320.3, 7.07) * mm});
            skLineSegment(sketch, "E124.3.0.27", {"start": v(342.25, -10.99) * mm, "end": v(342.25, 10.99) * mm});
            skLineSegment(sketch, "E124.3.0.28", {"start": v(339.73, -14.5) * mm, "end": v(324.48, -18.6) * mm});
            skLineSegment(sketch, "E124.3.0.29", {"start": v(279.75, -7.4) * mm, "end": v(279.75, -19.25) * mm});
            skLineSegment(sketch, "E124.3.0.30", {"start": v(324.48, 18.6) * mm, "end": v(339.73, 14.5) * mm});
            skLineSegment(sketch, "E124.3.0.31", {"start": v(275.74, -15.8) * mm, "end": v(256.57, -10.67) * mm});
            skLineSegment(sketch, "E124.3.0.32", {"start": v(339, 42.25) * mm, "end": v(316.44, 42.25) * mm});
            skLineSegment(sketch, "E124.3.0.33", {"start": v(324.26, -15.8) * mm, "end": v(342.25, -10.99) * mm});
            skLineSegment(sketch, "E124.3.0.34", {"start": v(289.33, -43.43) * mm, "end": v(284.2, -24.26) * mm});
            skLineSegment(sketch, "E124.3.0.35", {"start": v(275.52, -18.6) * mm, "end": v(260.27, -14.5) * mm});
            skLineSegment(sketch, "E124.3.0.36", {"start": v(261, -42.25) * mm, "end": v(283.56, -42.25) * mm});
            skLineSegment(sketch, "E124.3.0.37", {"start": v(315.8, -24.26) * mm, "end": v(310.67, -43.43) * mm});
            skLineSegment(sketch, "E124.3.0.38", {"start": v(261, -45) * mm, "end": v(288.12, -45) * mm});
            skLineSegment(sketch, "E124.3.0.39", {"start": v(342.25, 10.99) * mm, "end": v(324.26, 15.8) * mm});
            skArc(sketch, "E124.3.0.40", {"start": v(279.7, 7.07) * mm, "mid": v(278.5, 0) * mm, "end": v(279.7, -7.07) * mm});
            skLineSegment(sketch, "E124.3.0.41", {"start": v(285.5, -39.73) * mm, "end": v(281.4, -24.48) * mm});
            skLineSegment(sketch, "E124.3.0.42", {"start": v(256.57, 10.67) * mm, "end": v(275.74, 15.8) * mm});
            skArc(sketch, "E124.3.0.43", {"start": v(345, 39) * mm, "mid": v(343.24, 43.24) * mm, "end": v(339, 45) * mm});
            skArc(sketch, "E124.3.0.44", {"start": v(291.14, -23.09) * mm, "mid": v(300, -25) * mm, "end": v(308.86, -23.09) * mm});
            skLineSegment(sketch, "E124.3.0.45", {"start": v(283.56, 42.25) * mm, "end": v(261, 42.25) * mm});
            skLineSegment(sketch, "E124.3.0.46", {"start": v(311.88, -45) * mm, "end": v(339, -45) * mm});
            skLineSegment(sketch, "E124.3.0.47", {"start": v(345, -39) * mm, "end": v(345, 39) * mm});
            skLineSegment(sketch, "E124.3.0.48", {"start": v(277, 14.84) * mm, "end": v(277, 9.27) * mm});
            skArc(sketch, "E124.3.0.49", {"start": v(257.75, 16.44) * mm, "mid": v(258.53, 14.85) * mm, "end": v(260.27, 14.5) * mm});
            skLineSegment(sketch, "E124.3.0.50", {"start": v(319.25, 20.25) * mm, "end": v(307.4, 20.25) * mm});
            skArc(sketch, "E124.3.0.51", {"start": v(314.84, 23) * mm, "mid": v(315.64, 23.4) * mm, "end": v(315.8, 24.26) * mm});
            skArc(sketch, "E124.3.0.52", {"start": v(284.2, 24.26) * mm, "mid": v(284.36, 23.4) * mm, "end": v(285.16, 23) * mm});
            skArc(sketch, "E124.3.0.53", {"start": v(256.57, -10.67) * mm, "mid": v(255.49, -10.89) * mm, "end": v(255, -11.88) * mm});
            skArc(sketch, "E124.3.0.54", {"start": v(277, 14.84) * mm, "mid": v(276.6, 15.64) * mm, "end": v(275.74, 15.8) * mm});
            skArc(sketch, "E124.3.0.55", {"start": v(285.5, 39.73) * mm, "mid": v(285.15, 41.47) * mm, "end": v(283.56, 42.25) * mm});
            skArc(sketch, "E124.3.0.56", {"start": v(339, -42.25) * mm, "mid": v(341.3, -41.3) * mm, "end": v(342.25, -39) * mm});
            skLineSegment(sketch, "E124.3.0.57", {"start": v(307.4, -20.25) * mm, "end": v(319.25, -20.25) * mm});
            skArc(sketch, "E124.3.0.58", {"start": v(261, 42.25) * mm, "mid": v(258.7, 41.3) * mm, "end": v(257.75, 39) * mm});
            skArc(sketch, "E124.3.0.59", {"start": v(283.56, -42.25) * mm, "mid": v(285.15, -41.47) * mm, "end": v(285.5, -39.73) * mm});
            skLineSegment(sketch, "E124.3.0.60", {"start": v(280.75, -20.25) * mm, "end": v(292.6, -20.25) * mm});
            skArc(sketch, "E124.3.0.61", {"start": v(323, -14.84) * mm, "mid": v(323.4, -15.64) * mm, "end": v(324.26, -15.8) * mm});
            skArc(sketch, "E124.3.0.62", {"start": v(342.25, -16.44) * mm, "mid": v(341.47, -14.85) * mm, "end": v(339.73, -14.5) * mm});
            skLineSegment(sketch, "E124.3.0.63", {"start": v(323, 14.84) * mm, "end": v(323, 9.27) * mm});
            skArc(sketch, "E124.3.0.64", {"start": v(260.27, -14.5) * mm, "mid": v(258.53, -14.85) * mm, "end": v(257.75, -16.44) * mm});
            skArc(sketch, "E124.3.0.65", {"start": v(316.44, 42.25) * mm, "mid": v(314.85, 41.47) * mm, "end": v(314.5, 39.73) * mm});
            skArc(sketch, "E124.3.0.66", {"start": v(310.67, -43.43) * mm, "mid": v(310.89, -44.51) * mm, "end": v(311.88, -45) * mm});
            skArc(sketch, "E124.3.0.67", {"start": v(318.6, 24.48) * mm, "mid": v(319.3, 23.41) * mm, "end": v(320.53, 23) * mm});
            skLineSegment(sketch, "E124.3.0.68", {"start": v(277, -9.27) * mm, "end": v(277, -14.84) * mm});
            skArc(sketch, "E124.3.0.69", {"start": v(275.74, -15.8) * mm, "mid": v(276.6, -15.64) * mm, "end": v(277, -14.84) * mm});
            skLineSegment(sketch, "E124.3.0.70", {"start": v(323, -9.27) * mm, "end": v(323, -14.84) * mm});
            skLineSegment(sketch, "E124.3.0.71", {"start": v(309.27, 23) * mm, "end": v(314.84, 23) * mm});
            skArc(sketch, "E124.3.0.72", {"start": v(255, 11.88) * mm, "mid": v(255.49, 10.89) * mm, "end": v(256.57, 10.67) * mm});
            skArc(sketch, "E124.3.0.73", {"start": v(339.73, 14.5) * mm, "mid": v(341.47, 14.85) * mm, "end": v(342.25, 16.44) * mm});
            skLineSegment(sketch, "E124.3.0.74", {"start": v(292.6, 20.25) * mm, "end": v(280.75, 20.25) * mm});
            skArc(sketch, "E124.3.0.75", {"start": v(314.5, -39.73) * mm, "mid": v(314.85, -41.47) * mm, "end": v(316.44, -42.25) * mm});
            skLineSegment(sketch, "E124.3.0.76", {"start": v(309.27, -23) * mm, "end": v(314.84, -23) * mm});
            skLineSegment(sketch, "E124.3.0.77", {"start": v(285.16, 23) * mm, "end": v(290.73, 23) * mm});
            skArc(sketch, "E124.3.0.78", {"start": v(320.25, 19.25) * mm, "mid": v(319.96, 19.96) * mm, "end": v(319.25, 20.25) * mm});
            skArc(sketch, "E124.3.0.79", {"start": v(342.25, 39) * mm, "mid": v(341.3, 41.3) * mm, "end": v(339, 42.25) * mm});
            skArc(sketch, "E124.3.0.80", {"start": v(320.53, -23) * mm, "mid": v(319.3, -23.41) * mm, "end": v(318.6, -24.48) * mm});
            skArc(sketch, "E124.3.0.81", {"start": v(279.47, 23) * mm, "mid": v(280.7, 23.41) * mm, "end": v(281.4, 24.48) * mm});
            skArc(sketch, "E124.3.0.82", {"start": v(315.8, -24.26) * mm, "mid": v(315.64, -23.4) * mm, "end": v(314.84, -23) * mm});
            skArc(sketch, "E124.3.0.83", {"start": v(285.16, -23) * mm, "mid": v(284.36, -23.4) * mm, "end": v(284.2, -24.26) * mm});
            skArc(sketch, "E124.3.0.84", {"start": v(319.25, -20.25) * mm, "mid": v(319.96, -19.96) * mm, "end": v(320.25, -19.25) * mm});
            skArc(sketch, "E124.3.0.85", {"start": v(279.75, -19.25) * mm, "mid": v(280.04, -19.96) * mm, "end": v(280.75, -20.25) * mm});
            skArc(sketch, "E124.3.0.86", {"start": v(280.75, 20.25) * mm, "mid": v(280.04, 19.96) * mm, "end": v(279.75, 19.25) * mm});
            skArc(sketch, "E124.3.0.87", {"start": v(288.12, -45) * mm, "mid": v(289.11, -44.51) * mm, "end": v(289.33, -43.43) * mm});
            skLineSegment(sketch, "E124.3.0.88", {"start": v(285.16, -23) * mm, "end": v(290.73, -23) * mm});
            skArc(sketch, "E124.3.0.89", {"start": v(281.4, -24.48) * mm, "mid": v(280.7, -23.41) * mm, "end": v(279.47, -23) * mm});
            skArc(sketch, "E124.3.0.90", {"start": v(257.75, -39) * mm, "mid": v(258.7, -41.3) * mm, "end": v(261, -42.25) * mm});
            skArc(sketch, "E124.3.0.91", {"start": v(324.26, 15.8) * mm, "mid": v(323.4, 15.64) * mm, "end": v(323, 14.84) * mm});
            skArc(sketch, "E124.3.0.92", {"start": v(323.09, -8.86) * mm, "mid": v(323.02, -9.06) * mm, "end": v(323, -9.27) * mm});
            skArc(sketch, "E124.3.0.93", {"start": v(277, -20.53) * mm, "mid": v(276.59, -19.3) * mm, "end": v(275.52, -18.6) * mm});
            skArc(sketch, "E124.3.0.94", {"start": v(277, -21) * mm, "mid": v(277.59, -22.41) * mm, "end": v(279, -23) * mm});
            skLineSegment(sketch, "E124.3.0.95", {"start": v(279, 23) * mm, "end": v(279.47, 23) * mm});
            skArc(sketch, "E124.3.0.96", {"start": v(308.86, 23.09) * mm, "mid": v(309.06, 23.02) * mm, "end": v(309.27, 23) * mm});
            skArc(sketch, "E124.3.0.97", {"start": v(323, 9.27) * mm, "mid": v(323.02, 9.06) * mm, "end": v(323.09, 8.86) * mm});
            skArc(sketch, "E124.3.0.98", {"start": v(320.25, 7.4) * mm, "mid": v(320.26, 7.23) * mm, "end": v(320.3, 7.07) * mm});
            skArc(sketch, "E124.3.0.99", {"start": v(279, 23) * mm, "mid": v(277.59, 22.41) * mm, "end": v(277, 21) * mm});
            skArc(sketch, "E124.3.0.100", {"start": v(279.75, -7.4) * mm, "mid": v(279.74, -7.23) * mm, "end": v(279.7, -7.07) * mm});
            skArc(sketch, "E124.3.0.101", {"start": v(276.91, 8.86) * mm, "mid": v(276.98, 9.06) * mm, "end": v(277, 9.27) * mm});
            skArc(sketch, "E124.3.0.102", {"start": v(292.6, 20.25) * mm, "mid": v(292.77, 20.26) * mm, "end": v(292.93, 20.3) * mm});
            skLineSegment(sketch, "E124.3.0.103", {"start": v(279.47, -23) * mm, "end": v(279, -23) * mm});
            skArc(sketch, "E124.3.0.104", {"start": v(320.3, -7.07) * mm, "mid": v(320.26, -7.23) * mm, "end": v(320.25, -7.4) * mm});
            skArc(sketch, "E124.3.0.105", {"start": v(279.7, 7.07) * mm, "mid": v(279.74, 7.23) * mm, "end": v(279.75, 7.4) * mm});
            skArc(sketch, "E124.3.0.106", {"start": v(290.73, 23) * mm, "mid": v(290.94, 23.02) * mm, "end": v(291.14, 23.09) * mm});
            skLineSegment(sketch, "E124.3.0.107", {"start": v(277, -21) * mm, "end": v(277, -20.53) * mm});
            skArc(sketch, "E124.3.0.108", {"start": v(275.52, 18.6) * mm, "mid": v(276.59, 19.3) * mm, "end": v(277, 20.53) * mm});
            skArc(sketch, "E124.3.0.109", {"start": v(277, -9.27) * mm, "mid": v(276.98, -9.06) * mm, "end": v(276.91, -8.86) * mm});
            skArc(sketch, "E124.3.0.110", {"start": v(307.07, 20.3) * mm, "mid": v(307.23, 20.26) * mm, "end": v(307.4, 20.25) * mm});
            skLineSegment(sketch, "E124.3.0.111", {"start": v(320.53, 23) * mm, "end": v(321, 23) * mm});
            skArc(sketch, "E124.3.0.112", {"start": v(324.48, -18.6) * mm, "mid": v(323.41, -19.3) * mm, "end": v(323, -20.53) * mm});
            skArc(sketch, "E124.3.0.113", {"start": v(307.4, -20.25) * mm, "mid": v(307.23, -20.26) * mm, "end": v(307.07, -20.3) * mm});
            skArc(sketch, "E124.3.0.114", {"start": v(321, -23) * mm, "mid": v(322.41, -22.41) * mm, "end": v(323, -21) * mm});
            skLineSegment(sketch, "E124.3.0.115", {"start": v(321, -23) * mm, "end": v(320.53, -23) * mm});
            skLineSegment(sketch, "E124.3.0.116", {"start": v(323, -20.53) * mm, "end": v(323, -21) * mm});
            skArc(sketch, "E124.3.0.117", {"start": v(309.27, -23) * mm, "mid": v(309.06, -23.02) * mm, "end": v(308.86, -23.09) * mm});
            skArc(sketch, "E124.3.0.118", {"start": v(291.14, -23.09) * mm, "mid": v(290.94, -23.02) * mm, "end": v(290.73, -23) * mm});
            skArc(sketch, "E124.3.0.119", {"start": v(323, 20.53) * mm, "mid": v(323.41, 19.3) * mm, "end": v(324.48, 18.6) * mm});
            skArc(sketch, "E124.3.0.120", {"start": v(292.93, -20.3) * mm, "mid": v(292.77, -20.26) * mm, "end": v(292.6, -20.25) * mm});
            skLineSegment(sketch, "E124.3.0.121", {"start": v(277, 20.53) * mm, "end": v(277, 21) * mm});
            skArc(sketch, "E124.3.0.122", {"start": v(323, 21) * mm, "mid": v(322.41, 22.41) * mm, "end": v(321, 23) * mm});
            skLineSegment(sketch, "E124.3.0.123", {"start": v(323, 21) * mm, "end": v(323, 20.53) * mm});
            skLineSegment(sketch, "E124.4.0.0", {"start": v(357.75, 39) * mm, "end": v(357.75, 16.44) * mm});
            skLineSegment(sketch, "E124.4.0.1", {"start": v(415.8, 24.26) * mm, "end": v(410.99, 42.25) * mm});
            skLineSegment(sketch, "E124.4.0.2", {"start": v(389.01, 42.25) * mm, "end": v(384.2, 24.26) * mm});
            skArc(sketch, "E124.4.0.3", {"start": v(407.07, 20.3) * mm, "mid": v(400, 21.5) * mm, "end": v(392.93, 20.3) * mm});
            skLineSegment(sketch, "E124.4.0.4", {"start": v(360.27, 14.5) * mm, "end": v(375.52, 18.6) * mm});
            skLineSegment(sketch, "E124.4.0.5", {"start": v(381.4, 24.48) * mm, "end": v(385.5, 39.73) * mm});
            skLineSegment(sketch, "E124.4.0.6", {"start": v(439, 45) * mm, "end": v(361, 45) * mm});
            skArc(sketch, "E124.4.0.7", {"start": v(439, -45) * mm, "mid": v(443.24, -43.24) * mm, "end": v(445, -39) * mm});
            skArc(sketch, "E124.4.0.8", {"start": v(392.93, -20.3) * mm, "mid": v(400, -21.5) * mm, "end": v(407.07, -20.3) * mm});
            skLineSegment(sketch, "E124.4.0.9", {"start": v(420.25, -19.25) * mm, "end": v(420.25, -7.4) * mm});
            skLineSegment(sketch, "E124.4.0.10", {"start": v(379.75, 19.25) * mm, "end": v(379.75, 7.4) * mm});
            skLineSegment(sketch, "E124.4.0.11", {"start": v(418.6, -24.48) * mm, "end": v(414.5, -39.73) * mm});
            skArc(sketch, "E124.4.0.12", {"start": v(376.91, 8.86) * mm, "mid": v(375, 0) * mm, "end": v(376.91, -8.86) * mm});
            skLineSegment(sketch, "E124.4.0.13", {"start": v(414.5, 39.73) * mm, "end": v(418.6, 24.48) * mm});
            skLineSegment(sketch, "E124.4.0.14", {"start": v(416.44, -42.25) * mm, "end": v(439, -42.25) * mm});
            skLineSegment(sketch, "E124.4.0.15", {"start": v(410.99, 42.25) * mm, "end": v(389.01, 42.25) * mm});
            skLineSegment(sketch, "E124.4.0.16", {"start": v(355, 39) * mm, "end": v(355, 11.88) * mm});
            skLineSegment(sketch, "E124.4.0.17", {"start": v(420.25, 7.4) * mm, "end": v(420.25, 19.25) * mm});
            skLineSegment(sketch, "E124.4.0.18", {"start": v(355, -11.88) * mm, "end": v(355, -39) * mm});
            skLineSegment(sketch, "E124.4.0.19", {"start": v(442.25, -39) * mm, "end": v(442.25, -16.44) * mm});
            skLineSegment(sketch, "E124.4.0.20", {"start": v(357.75, -16.44) * mm, "end": v(357.75, -39) * mm});
            skArc(sketch, "E124.4.0.21", {"start": v(361, 45) * mm, "mid": v(356.76, 43.24) * mm, "end": v(355, 39) * mm});
            skArc(sketch, "E124.4.0.22", {"start": v(423.09, -8.86) * mm, "mid": v(425, 0) * mm, "end": v(423.09, 8.86) * mm});
            skArc(sketch, "E124.4.0.23", {"start": v(408.86, 23.09) * mm, "mid": v(400, 25) * mm, "end": v(391.14, 23.09) * mm});
            skLineSegment(sketch, "E124.4.0.24", {"start": v(442.25, 16.44) * mm, "end": v(442.25, 39) * mm});
            skArc(sketch, "E124.4.0.25", {"start": v(355, -39) * mm, "mid": v(356.76, -43.24) * mm, "end": v(361, -45) * mm});
            skArc(sketch, "E124.4.0.26", {"start": v(420.3, -7.07) * mm, "mid": v(421.5, 0) * mm, "end": v(420.3, 7.07) * mm});
            skLineSegment(sketch, "E124.4.0.27", {"start": v(442.25, -10.99) * mm, "end": v(442.25, 10.99) * mm});
            skLineSegment(sketch, "E124.4.0.28", {"start": v(439.73, -14.5) * mm, "end": v(424.48, -18.6) * mm});
            skLineSegment(sketch, "E124.4.0.29", {"start": v(379.75, -7.4) * mm, "end": v(379.75, -19.25) * mm});
            skLineSegment(sketch, "E124.4.0.30", {"start": v(424.48, 18.6) * mm, "end": v(439.73, 14.5) * mm});
            skLineSegment(sketch, "E124.4.0.31", {"start": v(375.74, -15.8) * mm, "end": v(356.57, -10.67) * mm});
            skLineSegment(sketch, "E124.4.0.32", {"start": v(439, 42.25) * mm, "end": v(416.44, 42.25) * mm});
            skLineSegment(sketch, "E124.4.0.33", {"start": v(424.26, -15.8) * mm, "end": v(442.25, -10.99) * mm});
            skLineSegment(sketch, "E124.4.0.34", {"start": v(389.33, -43.43) * mm, "end": v(384.2, -24.26) * mm});
            skLineSegment(sketch, "E124.4.0.35", {"start": v(375.52, -18.6) * mm, "end": v(360.27, -14.5) * mm});
            skLineSegment(sketch, "E124.4.0.36", {"start": v(361, -42.25) * mm, "end": v(383.56, -42.25) * mm});
            skLineSegment(sketch, "E124.4.0.37", {"start": v(415.8, -24.26) * mm, "end": v(410.67, -43.43) * mm});
            skLineSegment(sketch, "E124.4.0.38", {"start": v(361, -45) * mm, "end": v(388.12, -45) * mm});
            skLineSegment(sketch, "E124.4.0.39", {"start": v(442.25, 10.99) * mm, "end": v(424.26, 15.8) * mm});
            skArc(sketch, "E124.4.0.40", {"start": v(379.7, 7.07) * mm, "mid": v(378.5, 0) * mm, "end": v(379.7, -7.07) * mm});
            skLineSegment(sketch, "E124.4.0.41", {"start": v(385.5, -39.73) * mm, "end": v(381.4, -24.48) * mm});
            skLineSegment(sketch, "E124.4.0.42", {"start": v(356.57, 10.67) * mm, "end": v(375.74, 15.8) * mm});
            skArc(sketch, "E124.4.0.43", {"start": v(445, 39) * mm, "mid": v(443.24, 43.24) * mm, "end": v(439, 45) * mm});
            skArc(sketch, "E124.4.0.44", {"start": v(391.14, -23.09) * mm, "mid": v(400, -25) * mm, "end": v(408.86, -23.09) * mm});
            skLineSegment(sketch, "E124.4.0.45", {"start": v(383.56, 42.25) * mm, "end": v(361, 42.25) * mm});
            skLineSegment(sketch, "E124.4.0.46", {"start": v(411.88, -45) * mm, "end": v(439, -45) * mm});
            skLineSegment(sketch, "E124.4.0.47", {"start": v(445, -39) * mm, "end": v(445, 39) * mm});
            skLineSegment(sketch, "E124.4.0.48", {"start": v(377, 14.84) * mm, "end": v(377, 9.27) * mm});
            skArc(sketch, "E124.4.0.49", {"start": v(357.75, 16.44) * mm, "mid": v(358.53, 14.85) * mm, "end": v(360.27, 14.5) * mm});
            skLineSegment(sketch, "E124.4.0.50", {"start": v(419.25, 20.25) * mm, "end": v(407.4, 20.25) * mm});
            skArc(sketch, "E124.4.0.51", {"start": v(414.84, 23) * mm, "mid": v(415.64, 23.4) * mm, "end": v(415.8, 24.26) * mm});
            skArc(sketch, "E124.4.0.52", {"start": v(384.2, 24.26) * mm, "mid": v(384.36, 23.4) * mm, "end": v(385.16, 23) * mm});
            skArc(sketch, "E124.4.0.53", {"start": v(356.57, -10.67) * mm, "mid": v(355.49, -10.89) * mm, "end": v(355, -11.88) * mm});
            skArc(sketch, "E124.4.0.54", {"start": v(377, 14.84) * mm, "mid": v(376.6, 15.64) * mm, "end": v(375.74, 15.8) * mm});
            skArc(sketch, "E124.4.0.55", {"start": v(385.5, 39.73) * mm, "mid": v(385.15, 41.47) * mm, "end": v(383.56, 42.25) * mm});
            skArc(sketch, "E124.4.0.56", {"start": v(439, -42.25) * mm, "mid": v(441.3, -41.3) * mm, "end": v(442.25, -39) * mm});
            skLineSegment(sketch, "E124.4.0.57", {"start": v(407.4, -20.25) * mm, "end": v(419.25, -20.25) * mm});
            skArc(sketch, "E124.4.0.58", {"start": v(361, 42.25) * mm, "mid": v(358.7, 41.3) * mm, "end": v(357.75, 39) * mm});
            skArc(sketch, "E124.4.0.59", {"start": v(383.56, -42.25) * mm, "mid": v(385.15, -41.47) * mm, "end": v(385.5, -39.73) * mm});
            skLineSegment(sketch, "E124.4.0.60", {"start": v(380.75, -20.25) * mm, "end": v(392.6, -20.25) * mm});
            skArc(sketch, "E124.4.0.61", {"start": v(423, -14.84) * mm, "mid": v(423.4, -15.64) * mm, "end": v(424.26, -15.8) * mm});
            skArc(sketch, "E124.4.0.62", {"start": v(442.25, -16.44) * mm, "mid": v(441.47, -14.85) * mm, "end": v(439.73, -14.5) * mm});
            skLineSegment(sketch, "E124.4.0.63", {"start": v(423, 14.84) * mm, "end": v(423, 9.27) * mm});
            skArc(sketch, "E124.4.0.64", {"start": v(360.27, -14.5) * mm, "mid": v(358.53, -14.85) * mm, "end": v(357.75, -16.44) * mm});
            skArc(sketch, "E124.4.0.65", {"start": v(416.44, 42.25) * mm, "mid": v(414.85, 41.47) * mm, "end": v(414.5, 39.73) * mm});
            skArc(sketch, "E124.4.0.66", {"start": v(410.67, -43.43) * mm, "mid": v(410.89, -44.51) * mm, "end": v(411.88, -45) * mm});
            skArc(sketch, "E124.4.0.67", {"start": v(418.6, 24.48) * mm, "mid": v(419.3, 23.41) * mm, "end": v(420.53, 23) * mm});
            skLineSegment(sketch, "E124.4.0.68", {"start": v(377, -9.27) * mm, "end": v(377, -14.84) * mm});
            skArc(sketch, "E124.4.0.69", {"start": v(375.74, -15.8) * mm, "mid": v(376.6, -15.64) * mm, "end": v(377, -14.84) * mm});
            skLineSegment(sketch, "E124.4.0.70", {"start": v(423, -9.27) * mm, "end": v(423, -14.84) * mm});
            skLineSegment(sketch, "E124.4.0.71", {"start": v(409.27, 23) * mm, "end": v(414.84, 23) * mm});
            skArc(sketch, "E124.4.0.72", {"start": v(355, 11.88) * mm, "mid": v(355.49, 10.89) * mm, "end": v(356.57, 10.67) * mm});
            skArc(sketch, "E124.4.0.73", {"start": v(439.73, 14.5) * mm, "mid": v(441.47, 14.85) * mm, "end": v(442.25, 16.44) * mm});
            skLineSegment(sketch, "E124.4.0.74", {"start": v(392.6, 20.25) * mm, "end": v(380.75, 20.25) * mm});
            skArc(sketch, "E124.4.0.75", {"start": v(414.5, -39.73) * mm, "mid": v(414.85, -41.47) * mm, "end": v(416.44, -42.25) * mm});
            skLineSegment(sketch, "E124.4.0.76", {"start": v(409.27, -23) * mm, "end": v(414.84, -23) * mm});
            skLineSegment(sketch, "E124.4.0.77", {"start": v(385.16, 23) * mm, "end": v(390.73, 23) * mm});
            skArc(sketch, "E124.4.0.78", {"start": v(420.25, 19.25) * mm, "mid": v(419.96, 19.96) * mm, "end": v(419.25, 20.25) * mm});
            skArc(sketch, "E124.4.0.79", {"start": v(442.25, 39) * mm, "mid": v(441.3, 41.3) * mm, "end": v(439, 42.25) * mm});
            skArc(sketch, "E124.4.0.80", {"start": v(420.53, -23) * mm, "mid": v(419.3, -23.41) * mm, "end": v(418.6, -24.48) * mm});
            skArc(sketch, "E124.4.0.81", {"start": v(379.47, 23) * mm, "mid": v(380.7, 23.41) * mm, "end": v(381.4, 24.48) * mm});
            skArc(sketch, "E124.4.0.82", {"start": v(415.8, -24.26) * mm, "mid": v(415.64, -23.4) * mm, "end": v(414.84, -23) * mm});
            skArc(sketch, "E124.4.0.83", {"start": v(385.16, -23) * mm, "mid": v(384.36, -23.4) * mm, "end": v(384.2, -24.26) * mm});
            skArc(sketch, "E124.4.0.84", {"start": v(419.25, -20.25) * mm, "mid": v(419.96, -19.96) * mm, "end": v(420.25, -19.25) * mm});
            skArc(sketch, "E124.4.0.85", {"start": v(379.75, -19.25) * mm, "mid": v(380.04, -19.96) * mm, "end": v(380.75, -20.25) * mm});
            skArc(sketch, "E124.4.0.86", {"start": v(380.75, 20.25) * mm, "mid": v(380.04, 19.96) * mm, "end": v(379.75, 19.25) * mm});
            skArc(sketch, "E124.4.0.87", {"start": v(388.12, -45) * mm, "mid": v(389.11, -44.51) * mm, "end": v(389.33, -43.43) * mm});
            skLineSegment(sketch, "E124.4.0.88", {"start": v(385.16, -23) * mm, "end": v(390.73, -23) * mm});
            skArc(sketch, "E124.4.0.89", {"start": v(381.4, -24.48) * mm, "mid": v(380.7, -23.41) * mm, "end": v(379.47, -23) * mm});
            skArc(sketch, "E124.4.0.90", {"start": v(357.75, -39) * mm, "mid": v(358.7, -41.3) * mm, "end": v(361, -42.25) * mm});
            skArc(sketch, "E124.4.0.91", {"start": v(424.26, 15.8) * mm, "mid": v(423.4, 15.64) * mm, "end": v(423, 14.84) * mm});
            skArc(sketch, "E124.4.0.92", {"start": v(423.09, -8.86) * mm, "mid": v(423.02, -9.06) * mm, "end": v(423, -9.27) * mm});
            skArc(sketch, "E124.4.0.93", {"start": v(377, -20.53) * mm, "mid": v(376.59, -19.3) * mm, "end": v(375.52, -18.6) * mm});
            skArc(sketch, "E124.4.0.94", {"start": v(377, -21) * mm, "mid": v(377.59, -22.41) * mm, "end": v(379, -23) * mm});
            skLineSegment(sketch, "E124.4.0.95", {"start": v(379, 23) * mm, "end": v(379.47, 23) * mm});
            skArc(sketch, "E124.4.0.96", {"start": v(408.86, 23.09) * mm, "mid": v(409.06, 23.02) * mm, "end": v(409.27, 23) * mm});
            skArc(sketch, "E124.4.0.97", {"start": v(423, 9.27) * mm, "mid": v(423.02, 9.06) * mm, "end": v(423.09, 8.86) * mm});
            skArc(sketch, "E124.4.0.98", {"start": v(420.25, 7.4) * mm, "mid": v(420.26, 7.23) * mm, "end": v(420.3, 7.07) * mm});
            skArc(sketch, "E124.4.0.99", {"start": v(379, 23) * mm, "mid": v(377.59, 22.41) * mm, "end": v(377, 21) * mm});
            skArc(sketch, "E124.4.0.100", {"start": v(379.75, -7.4) * mm, "mid": v(379.74, -7.23) * mm, "end": v(379.7, -7.07) * mm});
            skArc(sketch, "E124.4.0.101", {"start": v(376.91, 8.86) * mm, "mid": v(376.98, 9.06) * mm, "end": v(377, 9.27) * mm});
            skArc(sketch, "E124.4.0.102", {"start": v(392.6, 20.25) * mm, "mid": v(392.77, 20.26) * mm, "end": v(392.93, 20.3) * mm});
            skLineSegment(sketch, "E124.4.0.103", {"start": v(379.47, -23) * mm, "end": v(379, -23) * mm});
            skArc(sketch, "E124.4.0.104", {"start": v(420.3, -7.07) * mm, "mid": v(420.26, -7.23) * mm, "end": v(420.25, -7.4) * mm});
            skArc(sketch, "E124.4.0.105", {"start": v(379.7, 7.07) * mm, "mid": v(379.74, 7.23) * mm, "end": v(379.75, 7.4) * mm});
            skArc(sketch, "E124.4.0.106", {"start": v(390.73, 23) * mm, "mid": v(390.94, 23.02) * mm, "end": v(391.14, 23.09) * mm});
            skLineSegment(sketch, "E124.4.0.107", {"start": v(377, -21) * mm, "end": v(377, -20.53) * mm});
            skArc(sketch, "E124.4.0.108", {"start": v(375.52, 18.6) * mm, "mid": v(376.59, 19.3) * mm, "end": v(377, 20.53) * mm});
            skArc(sketch, "E124.4.0.109", {"start": v(377, -9.27) * mm, "mid": v(376.98, -9.06) * mm, "end": v(376.91, -8.86) * mm});
            skArc(sketch, "E124.4.0.110", {"start": v(407.07, 20.3) * mm, "mid": v(407.23, 20.26) * mm, "end": v(407.4, 20.25) * mm});
            skLineSegment(sketch, "E124.4.0.111", {"start": v(420.53, 23) * mm, "end": v(421, 23) * mm});
            skArc(sketch, "E124.4.0.112", {"start": v(424.48, -18.6) * mm, "mid": v(423.41, -19.3) * mm, "end": v(423, -20.53) * mm});
            skArc(sketch, "E124.4.0.113", {"start": v(407.4, -20.25) * mm, "mid": v(407.23, -20.26) * mm, "end": v(407.07, -20.3) * mm});
            skArc(sketch, "E124.4.0.114", {"start": v(421, -23) * mm, "mid": v(422.41, -22.41) * mm, "end": v(423, -21) * mm});
            skLineSegment(sketch, "E124.4.0.115", {"start": v(421, -23) * mm, "end": v(420.53, -23) * mm});
            skLineSegment(sketch, "E124.4.0.116", {"start": v(423, -20.53) * mm, "end": v(423, -21) * mm});
            skArc(sketch, "E124.4.0.117", {"start": v(409.27, -23) * mm, "mid": v(409.06, -23.02) * mm, "end": v(408.86, -23.09) * mm});
            skArc(sketch, "E124.4.0.118", {"start": v(391.14, -23.09) * mm, "mid": v(390.94, -23.02) * mm, "end": v(390.73, -23) * mm});
            skArc(sketch, "E124.4.0.119", {"start": v(423, 20.53) * mm, "mid": v(423.41, 19.3) * mm, "end": v(424.48, 18.6) * mm});
            skArc(sketch, "E124.4.0.120", {"start": v(392.93, -20.3) * mm, "mid": v(392.77, -20.26) * mm, "end": v(392.6, -20.25) * mm});
            skLineSegment(sketch, "E124.4.0.121", {"start": v(377, 20.53) * mm, "end": v(377, 21) * mm});
            skArc(sketch, "E124.4.0.122", {"start": v(423, 21) * mm, "mid": v(422.41, 22.41) * mm, "end": v(421, 23) * mm});
            skLineSegment(sketch, "E124.4.0.123", {"start": v(423, 21) * mm, "end": v(423, 20.53) * mm});
            skLineSegment(sketch, "E124.5.0.0", {"start": v(457.75, 39) * mm, "end": v(457.75, 16.44) * mm});
            skLineSegment(sketch, "E124.5.0.1", {"start": v(515.8, 24.26) * mm, "end": v(510.99, 42.25) * mm});
            skLineSegment(sketch, "E124.5.0.2", {"start": v(489.01, 42.25) * mm, "end": v(484.2, 24.26) * mm});
            skArc(sketch, "E124.5.0.3", {"start": v(507.07, 20.3) * mm, "mid": v(500, 21.5) * mm, "end": v(492.93, 20.3) * mm});
            skLineSegment(sketch, "E124.5.0.4", {"start": v(460.27, 14.5) * mm, "end": v(475.52, 18.6) * mm});
            skLineSegment(sketch, "E124.5.0.5", {"start": v(481.4, 24.48) * mm, "end": v(485.5, 39.73) * mm});
            skLineSegment(sketch, "E124.5.0.6", {"start": v(539, 45) * mm, "end": v(461, 45) * mm});
            skArc(sketch, "E124.5.0.7", {"start": v(539, -45) * mm, "mid": v(543.24, -43.24) * mm, "end": v(545, -39) * mm});
            skArc(sketch, "E124.5.0.8", {"start": v(492.93, -20.3) * mm, "mid": v(500, -21.5) * mm, "end": v(507.07, -20.3) * mm});
            skLineSegment(sketch, "E124.5.0.9", {"start": v(520.25, -19.25) * mm, "end": v(520.25, -7.4) * mm});
            skLineSegment(sketch, "E124.5.0.10", {"start": v(479.75, 19.25) * mm, "end": v(479.75, 7.4) * mm});
            skLineSegment(sketch, "E124.5.0.11", {"start": v(518.6, -24.48) * mm, "end": v(514.5, -39.73) * mm});
            skArc(sketch, "E124.5.0.12", {"start": v(476.91, 8.86) * mm, "mid": v(475, 0) * mm, "end": v(476.91, -8.86) * mm});
            skLineSegment(sketch, "E124.5.0.13", {"start": v(514.5, 39.73) * mm, "end": v(518.6, 24.48) * mm});
            skLineSegment(sketch, "E124.5.0.14", {"start": v(516.44, -42.25) * mm, "end": v(539, -42.25) * mm});
            skLineSegment(sketch, "E124.5.0.15", {"start": v(510.99, 42.25) * mm, "end": v(489.01, 42.25) * mm});
            skLineSegment(sketch, "E124.5.0.16", {"start": v(455, 39) * mm, "end": v(455, 11.88) * mm});
            skLineSegment(sketch, "E124.5.0.17", {"start": v(520.25, 7.4) * mm, "end": v(520.25, 19.25) * mm});
            skLineSegment(sketch, "E124.5.0.18", {"start": v(455, -11.88) * mm, "end": v(455, -39) * mm});
            skLineSegment(sketch, "E124.5.0.19", {"start": v(542.25, -39) * mm, "end": v(542.25, -16.44) * mm});
            skLineSegment(sketch, "E124.5.0.20", {"start": v(457.75, -16.44) * mm, "end": v(457.75, -39) * mm});
            skArc(sketch, "E124.5.0.21", {"start": v(461, 45) * mm, "mid": v(456.76, 43.24) * mm, "end": v(455, 39) * mm});
            skArc(sketch, "E124.5.0.22", {"start": v(523.09, -8.86) * mm, "mid": v(525, 0) * mm, "end": v(523.09, 8.86) * mm});
            skArc(sketch, "E124.5.0.23", {"start": v(508.86, 23.09) * mm, "mid": v(500, 25) * mm, "end": v(491.14, 23.09) * mm});
            skLineSegment(sketch, "E124.5.0.24", {"start": v(542.25, 16.44) * mm, "end": v(542.25, 39) * mm});
            skArc(sketch, "E124.5.0.25", {"start": v(455, -39) * mm, "mid": v(456.76, -43.24) * mm, "end": v(461, -45) * mm});
            skArc(sketch, "E124.5.0.26", {"start": v(520.3, -7.07) * mm, "mid": v(521.5, 0) * mm, "end": v(520.3, 7.07) * mm});
            skLineSegment(sketch, "E124.5.0.27", {"start": v(542.25, -10.99) * mm, "end": v(542.25, 10.99) * mm});
            skLineSegment(sketch, "E124.5.0.28", {"start": v(539.73, -14.5) * mm, "end": v(524.48, -18.6) * mm});
            skLineSegment(sketch, "E124.5.0.29", {"start": v(479.75, -7.4) * mm, "end": v(479.75, -19.25) * mm});
            skLineSegment(sketch, "E124.5.0.30", {"start": v(524.48, 18.6) * mm, "end": v(539.73, 14.5) * mm});
            skLineSegment(sketch, "E124.5.0.31", {"start": v(475.74, -15.8) * mm, "end": v(456.57, -10.67) * mm});
            skLineSegment(sketch, "E124.5.0.32", {"start": v(539, 42.25) * mm, "end": v(516.44, 42.25) * mm});
            skLineSegment(sketch, "E124.5.0.33", {"start": v(524.26, -15.8) * mm, "end": v(542.25, -10.99) * mm});
            skLineSegment(sketch, "E124.5.0.34", {"start": v(489.33, -43.43) * mm, "end": v(484.2, -24.26) * mm});
            skLineSegment(sketch, "E124.5.0.35", {"start": v(475.52, -18.6) * mm, "end": v(460.27, -14.5) * mm});
            skLineSegment(sketch, "E124.5.0.36", {"start": v(461, -42.25) * mm, "end": v(483.56, -42.25) * mm});
            skLineSegment(sketch, "E124.5.0.37", {"start": v(515.8, -24.26) * mm, "end": v(510.67, -43.43) * mm});
            skLineSegment(sketch, "E124.5.0.38", {"start": v(461, -45) * mm, "end": v(488.12, -45) * mm});
            skLineSegment(sketch, "E124.5.0.39", {"start": v(542.25, 10.99) * mm, "end": v(524.26, 15.8) * mm});
            skArc(sketch, "E124.5.0.40", {"start": v(479.7, 7.07) * mm, "mid": v(478.5, 0) * mm, "end": v(479.7, -7.07) * mm});
            skLineSegment(sketch, "E124.5.0.41", {"start": v(485.5, -39.73) * mm, "end": v(481.4, -24.48) * mm});
            skLineSegment(sketch, "E124.5.0.42", {"start": v(456.57, 10.67) * mm, "end": v(475.74, 15.8) * mm});
            skArc(sketch, "E124.5.0.43", {"start": v(545, 39) * mm, "mid": v(543.24, 43.24) * mm, "end": v(539, 45) * mm});
            skArc(sketch, "E124.5.0.44", {"start": v(491.14, -23.09) * mm, "mid": v(500, -25) * mm, "end": v(508.86, -23.09) * mm});
            skLineSegment(sketch, "E124.5.0.45", {"start": v(483.56, 42.25) * mm, "end": v(461, 42.25) * mm});
            skLineSegment(sketch, "E124.5.0.46", {"start": v(511.88, -45) * mm, "end": v(539, -45) * mm});
            skLineSegment(sketch, "E124.5.0.47", {"start": v(545, -39) * mm, "end": v(545, 39) * mm});
            skLineSegment(sketch, "E124.5.0.48", {"start": v(477, 14.84) * mm, "end": v(477, 9.27) * mm});
            skArc(sketch, "E124.5.0.49", {"start": v(457.75, 16.44) * mm, "mid": v(458.53, 14.85) * mm, "end": v(460.27, 14.5) * mm});
            skLineSegment(sketch, "E124.5.0.50", {"start": v(519.25, 20.25) * mm, "end": v(507.4, 20.25) * mm});
            skArc(sketch, "E124.5.0.51", {"start": v(514.84, 23) * mm, "mid": v(515.64, 23.4) * mm, "end": v(515.8, 24.26) * mm});
            skArc(sketch, "E124.5.0.52", {"start": v(484.2, 24.26) * mm, "mid": v(484.36, 23.4) * mm, "end": v(485.16, 23) * mm});
            skArc(sketch, "E124.5.0.53", {"start": v(456.57, -10.67) * mm, "mid": v(455.49, -10.89) * mm, "end": v(455, -11.88) * mm});
            skArc(sketch, "E124.5.0.54", {"start": v(477, 14.84) * mm, "mid": v(476.6, 15.64) * mm, "end": v(475.74, 15.8) * mm});
            skArc(sketch, "E124.5.0.55", {"start": v(485.5, 39.73) * mm, "mid": v(485.15, 41.47) * mm, "end": v(483.56, 42.25) * mm});
            skArc(sketch, "E124.5.0.56", {"start": v(539, -42.25) * mm, "mid": v(541.3, -41.3) * mm, "end": v(542.25, -39) * mm});
            skLineSegment(sketch, "E124.5.0.57", {"start": v(507.4, -20.25) * mm, "end": v(519.25, -20.25) * mm});
            skArc(sketch, "E124.5.0.58", {"start": v(461, 42.25) * mm, "mid": v(458.7, 41.3) * mm, "end": v(457.75, 39) * mm});
            skArc(sketch, "E124.5.0.59", {"start": v(483.56, -42.25) * mm, "mid": v(485.15, -41.47) * mm, "end": v(485.5, -39.73) * mm});
            skLineSegment(sketch, "E124.5.0.60", {"start": v(480.75, -20.25) * mm, "end": v(492.6, -20.25) * mm});
            skArc(sketch, "E124.5.0.61", {"start": v(523, -14.84) * mm, "mid": v(523.4, -15.64) * mm, "end": v(524.26, -15.8) * mm});
            skArc(sketch, "E124.5.0.62", {"start": v(542.25, -16.44) * mm, "mid": v(541.47, -14.85) * mm, "end": v(539.73, -14.5) * mm});
            skLineSegment(sketch, "E124.5.0.63", {"start": v(523, 14.84) * mm, "end": v(523, 9.27) * mm});
            skArc(sketch, "E124.5.0.64", {"start": v(460.27, -14.5) * mm, "mid": v(458.53, -14.85) * mm, "end": v(457.75, -16.44) * mm});
            skArc(sketch, "E124.5.0.65", {"start": v(516.44, 42.25) * mm, "mid": v(514.85, 41.47) * mm, "end": v(514.5, 39.73) * mm});
            skArc(sketch, "E124.5.0.66", {"start": v(510.67, -43.43) * mm, "mid": v(510.89, -44.51) * mm, "end": v(511.88, -45) * mm});
            skArc(sketch, "E124.5.0.67", {"start": v(518.6, 24.48) * mm, "mid": v(519.3, 23.41) * mm, "end": v(520.53, 23) * mm});
            skLineSegment(sketch, "E124.5.0.68", {"start": v(477, -9.27) * mm, "end": v(477, -14.84) * mm});
            skArc(sketch, "E124.5.0.69", {"start": v(475.74, -15.8) * mm, "mid": v(476.6, -15.64) * mm, "end": v(477, -14.84) * mm});
            skLineSegment(sketch, "E124.5.0.70", {"start": v(523, -9.27) * mm, "end": v(523, -14.84) * mm});
            skLineSegment(sketch, "E124.5.0.71", {"start": v(509.27, 23) * mm, "end": v(514.84, 23) * mm});
            skArc(sketch, "E124.5.0.72", {"start": v(455, 11.88) * mm, "mid": v(455.49, 10.89) * mm, "end": v(456.57, 10.67) * mm});
            skArc(sketch, "E124.5.0.73", {"start": v(539.73, 14.5) * mm, "mid": v(541.47, 14.85) * mm, "end": v(542.25, 16.44) * mm});
            skLineSegment(sketch, "E124.5.0.74", {"start": v(492.6, 20.25) * mm, "end": v(480.75, 20.25) * mm});
            skArc(sketch, "E124.5.0.75", {"start": v(514.5, -39.73) * mm, "mid": v(514.85, -41.47) * mm, "end": v(516.44, -42.25) * mm});
            skLineSegment(sketch, "E124.5.0.76", {"start": v(509.27, -23) * mm, "end": v(514.84, -23) * mm});
            skLineSegment(sketch, "E124.5.0.77", {"start": v(485.16, 23) * mm, "end": v(490.73, 23) * mm});
            skArc(sketch, "E124.5.0.78", {"start": v(520.25, 19.25) * mm, "mid": v(519.96, 19.96) * mm, "end": v(519.25, 20.25) * mm});
            skArc(sketch, "E124.5.0.79", {"start": v(542.25, 39) * mm, "mid": v(541.3, 41.3) * mm, "end": v(539, 42.25) * mm});
            skArc(sketch, "E124.5.0.80", {"start": v(520.53, -23) * mm, "mid": v(519.3, -23.41) * mm, "end": v(518.6, -24.48) * mm});
            skArc(sketch, "E124.5.0.81", {"start": v(479.47, 23) * mm, "mid": v(480.7, 23.41) * mm, "end": v(481.4, 24.48) * mm});
            skArc(sketch, "E124.5.0.82", {"start": v(515.8, -24.26) * mm, "mid": v(515.64, -23.4) * mm, "end": v(514.84, -23) * mm});
            skArc(sketch, "E124.5.0.83", {"start": v(485.16, -23) * mm, "mid": v(484.36, -23.4) * mm, "end": v(484.2, -24.26) * mm});
            skArc(sketch, "E124.5.0.84", {"start": v(519.25, -20.25) * mm, "mid": v(519.96, -19.96) * mm, "end": v(520.25, -19.25) * mm});
            skArc(sketch, "E124.5.0.85", {"start": v(479.75, -19.25) * mm, "mid": v(480.04, -19.96) * mm, "end": v(480.75, -20.25) * mm});
            skArc(sketch, "E124.5.0.86", {"start": v(480.75, 20.25) * mm, "mid": v(480.04, 19.96) * mm, "end": v(479.75, 19.25) * mm});
            skArc(sketch, "E124.5.0.87", {"start": v(488.12, -45) * mm, "mid": v(489.11, -44.51) * mm, "end": v(489.33, -43.43) * mm});
            skLineSegment(sketch, "E124.5.0.88", {"start": v(485.16, -23) * mm, "end": v(490.73, -23) * mm});
            skArc(sketch, "E124.5.0.89", {"start": v(481.4, -24.48) * mm, "mid": v(480.7, -23.41) * mm, "end": v(479.47, -23) * mm});
            skArc(sketch, "E124.5.0.90", {"start": v(457.75, -39) * mm, "mid": v(458.7, -41.3) * mm, "end": v(461, -42.25) * mm});
            skArc(sketch, "E124.5.0.91", {"start": v(524.26, 15.8) * mm, "mid": v(523.4, 15.64) * mm, "end": v(523, 14.84) * mm});
            skArc(sketch, "E124.5.0.92", {"start": v(523.09, -8.86) * mm, "mid": v(523.02, -9.06) * mm, "end": v(523, -9.27) * mm});
            skArc(sketch, "E124.5.0.93", {"start": v(477, -20.53) * mm, "mid": v(476.59, -19.3) * mm, "end": v(475.52, -18.6) * mm});
            skArc(sketch, "E124.5.0.94", {"start": v(477, -21) * mm, "mid": v(477.59, -22.41) * mm, "end": v(479, -23) * mm});
            skLineSegment(sketch, "E124.5.0.95", {"start": v(479, 23) * mm, "end": v(479.47, 23) * mm});
            skArc(sketch, "E124.5.0.96", {"start": v(508.86, 23.09) * mm, "mid": v(509.06, 23.02) * mm, "end": v(509.27, 23) * mm});
            skArc(sketch, "E124.5.0.97", {"start": v(523, 9.27) * mm, "mid": v(523.02, 9.06) * mm, "end": v(523.09, 8.86) * mm});
            skArc(sketch, "E124.5.0.98", {"start": v(520.25, 7.4) * mm, "mid": v(520.26, 7.23) * mm, "end": v(520.3, 7.07) * mm});
            skArc(sketch, "E124.5.0.99", {"start": v(479, 23) * mm, "mid": v(477.59, 22.41) * mm, "end": v(477, 21) * mm});
            skArc(sketch, "E124.5.0.100", {"start": v(479.75, -7.4) * mm, "mid": v(479.74, -7.23) * mm, "end": v(479.7, -7.07) * mm});
            skArc(sketch, "E124.5.0.101", {"start": v(476.91, 8.86) * mm, "mid": v(476.98, 9.06) * mm, "end": v(477, 9.27) * mm});
            skArc(sketch, "E124.5.0.102", {"start": v(492.6, 20.25) * mm, "mid": v(492.77, 20.26) * mm, "end": v(492.93, 20.3) * mm});
            skLineSegment(sketch, "E124.5.0.103", {"start": v(479.47, -23) * mm, "end": v(479, -23) * mm});
            skArc(sketch, "E124.5.0.104", {"start": v(520.3, -7.07) * mm, "mid": v(520.26, -7.23) * mm, "end": v(520.25, -7.4) * mm});
            skArc(sketch, "E124.5.0.105", {"start": v(479.7, 7.07) * mm, "mid": v(479.74, 7.23) * mm, "end": v(479.75, 7.4) * mm});
            skArc(sketch, "E124.5.0.106", {"start": v(490.73, 23) * mm, "mid": v(490.94, 23.02) * mm, "end": v(491.14, 23.09) * mm});
            skLineSegment(sketch, "E124.5.0.107", {"start": v(477, -21) * mm, "end": v(477, -20.53) * mm});
            skArc(sketch, "E124.5.0.108", {"start": v(475.52, 18.6) * mm, "mid": v(476.59, 19.3) * mm, "end": v(477, 20.53) * mm});
            skArc(sketch, "E124.5.0.109", {"start": v(477, -9.27) * mm, "mid": v(476.98, -9.06) * mm, "end": v(476.91, -8.86) * mm});
            skArc(sketch, "E124.5.0.110", {"start": v(507.07, 20.3) * mm, "mid": v(507.23, 20.26) * mm, "end": v(507.4, 20.25) * mm});
            skLineSegment(sketch, "E124.5.0.111", {"start": v(520.53, 23) * mm, "end": v(521, 23) * mm});
            skArc(sketch, "E124.5.0.112", {"start": v(524.48, -18.6) * mm, "mid": v(523.41, -19.3) * mm, "end": v(523, -20.53) * mm});
            skArc(sketch, "E124.5.0.113", {"start": v(507.4, -20.25) * mm, "mid": v(507.23, -20.26) * mm, "end": v(507.07, -20.3) * mm});
            skArc(sketch, "E124.5.0.114", {"start": v(521, -23) * mm, "mid": v(522.41, -22.41) * mm, "end": v(523, -21) * mm});
            skLineSegment(sketch, "E124.5.0.115", {"start": v(521, -23) * mm, "end": v(520.53, -23) * mm});
            skLineSegment(sketch, "E124.5.0.116", {"start": v(523, -20.53) * mm, "end": v(523, -21) * mm});
            skArc(sketch, "E124.5.0.117", {"start": v(509.27, -23) * mm, "mid": v(509.06, -23.02) * mm, "end": v(508.86, -23.09) * mm});
            skArc(sketch, "E124.5.0.118", {"start": v(491.14, -23.09) * mm, "mid": v(490.94, -23.02) * mm, "end": v(490.73, -23) * mm});
            skArc(sketch, "E124.5.0.119", {"start": v(523, 20.53) * mm, "mid": v(523.41, 19.3) * mm, "end": v(524.48, 18.6) * mm});
            skArc(sketch, "E124.5.0.120", {"start": v(492.93, -20.3) * mm, "mid": v(492.77, -20.26) * mm, "end": v(492.6, -20.25) * mm});
            skLineSegment(sketch, "E124.5.0.121", {"start": v(477, 20.53) * mm, "end": v(477, 21) * mm});
            skArc(sketch, "E124.5.0.122", {"start": v(523, 21) * mm, "mid": v(522.41, 22.41) * mm, "end": v(521, 23) * mm});
            skLineSegment(sketch, "E124.5.0.123", {"start": v(523, 21) * mm, "end": v(523, 20.53) * mm});
            skLineSegment(sketch, "E124.6.0.0", {"start": v(557.75, 39) * mm, "end": v(557.75, 16.44) * mm});
            skLineSegment(sketch, "E124.6.0.1", {"start": v(615.8, 24.26) * mm, "end": v(610.99, 42.25) * mm});
            skLineSegment(sketch, "E124.6.0.2", {"start": v(589.01, 42.25) * mm, "end": v(584.2, 24.26) * mm});
            skArc(sketch, "E124.6.0.3", {"start": v(607.07, 20.3) * mm, "mid": v(600, 21.5) * mm, "end": v(592.93, 20.3) * mm});
            skLineSegment(sketch, "E124.6.0.4", {"start": v(560.27, 14.5) * mm, "end": v(575.52, 18.6) * mm});
            skLineSegment(sketch, "E124.6.0.5", {"start": v(581.4, 24.48) * mm, "end": v(585.5, 39.73) * mm});
            skLineSegment(sketch, "E124.6.0.6", {"start": v(639, 45) * mm, "end": v(561, 45) * mm});
            skArc(sketch, "E124.6.0.7", {"start": v(639, -45) * mm, "mid": v(643.24, -43.24) * mm, "end": v(645, -39) * mm});
            skArc(sketch, "E124.6.0.8", {"start": v(592.93, -20.3) * mm, "mid": v(600, -21.5) * mm, "end": v(607.07, -20.3) * mm});
            skLineSegment(sketch, "E124.6.0.9", {"start": v(620.25, -19.25) * mm, "end": v(620.25, -7.4) * mm});
            skLineSegment(sketch, "E124.6.0.10", {"start": v(579.75, 19.25) * mm, "end": v(579.75, 7.4) * mm});
            skLineSegment(sketch, "E124.6.0.11", {"start": v(618.6, -24.48) * mm, "end": v(614.5, -39.73) * mm});
            skArc(sketch, "E124.6.0.12", {"start": v(576.91, 8.86) * mm, "mid": v(575, 0) * mm, "end": v(576.91, -8.86) * mm});
            skLineSegment(sketch, "E124.6.0.13", {"start": v(614.5, 39.73) * mm, "end": v(618.6, 24.48) * mm});
            skLineSegment(sketch, "E124.6.0.14", {"start": v(616.44, -42.25) * mm, "end": v(639, -42.25) * mm});
            skLineSegment(sketch, "E124.6.0.15", {"start": v(610.99, 42.25) * mm, "end": v(589.01, 42.25) * mm});
            skLineSegment(sketch, "E124.6.0.16", {"start": v(555, 39) * mm, "end": v(555, 11.88) * mm});
            skLineSegment(sketch, "E124.6.0.17", {"start": v(620.25, 7.4) * mm, "end": v(620.25, 19.25) * mm});
            skLineSegment(sketch, "E124.6.0.18", {"start": v(555, -11.88) * mm, "end": v(555, -39) * mm});
            skLineSegment(sketch, "E124.6.0.19", {"start": v(642.25, -39) * mm, "end": v(642.25, -16.44) * mm});
            skLineSegment(sketch, "E124.6.0.20", {"start": v(557.75, -16.44) * mm, "end": v(557.75, -39) * mm});
            skArc(sketch, "E124.6.0.21", {"start": v(561, 45) * mm, "mid": v(556.76, 43.24) * mm, "end": v(555, 39) * mm});
            skArc(sketch, "E124.6.0.22", {"start": v(623.09, -8.86) * mm, "mid": v(625, 0) * mm, "end": v(623.09, 8.86) * mm});
            skArc(sketch, "E124.6.0.23", {"start": v(608.86, 23.09) * mm, "mid": v(600, 25) * mm, "end": v(591.14, 23.09) * mm});
            skLineSegment(sketch, "E124.6.0.24", {"start": v(642.25, 16.44) * mm, "end": v(642.25, 39) * mm});
            skArc(sketch, "E124.6.0.25", {"start": v(555, -39) * mm, "mid": v(556.76, -43.24) * mm, "end": v(561, -45) * mm});
            skArc(sketch, "E124.6.0.26", {"start": v(620.3, -7.07) * mm, "mid": v(621.5, 0) * mm, "end": v(620.3, 7.07) * mm});
            skLineSegment(sketch, "E124.6.0.27", {"start": v(642.25, -10.99) * mm, "end": v(642.25, 10.99) * mm});
            skLineSegment(sketch, "E124.6.0.28", {"start": v(639.73, -14.5) * mm, "end": v(624.48, -18.6) * mm});
            skLineSegment(sketch, "E124.6.0.29", {"start": v(579.75, -7.4) * mm, "end": v(579.75, -19.25) * mm});
            skLineSegment(sketch, "E124.6.0.30", {"start": v(624.48, 18.6) * mm, "end": v(639.73, 14.5) * mm});
            skLineSegment(sketch, "E124.6.0.31", {"start": v(575.74, -15.8) * mm, "end": v(556.57, -10.67) * mm});
            skLineSegment(sketch, "E124.6.0.32", {"start": v(639, 42.25) * mm, "end": v(616.44, 42.25) * mm});
            skLineSegment(sketch, "E124.6.0.33", {"start": v(624.26, -15.8) * mm, "end": v(642.25, -10.99) * mm});
            skLineSegment(sketch, "E124.6.0.34", {"start": v(589.33, -43.43) * mm, "end": v(584.2, -24.26) * mm});
            skLineSegment(sketch, "E124.6.0.35", {"start": v(575.52, -18.6) * mm, "end": v(560.27, -14.5) * mm});
            skLineSegment(sketch, "E124.6.0.36", {"start": v(561, -42.25) * mm, "end": v(583.56, -42.25) * mm});
            skLineSegment(sketch, "E124.6.0.37", {"start": v(615.8, -24.26) * mm, "end": v(610.67, -43.43) * mm});
            skLineSegment(sketch, "E124.6.0.38", {"start": v(561, -45) * mm, "end": v(588.12, -45) * mm});
            skLineSegment(sketch, "E124.6.0.39", {"start": v(642.25, 10.99) * mm, "end": v(624.26, 15.8) * mm});
            skArc(sketch, "E124.6.0.40", {"start": v(579.7, 7.07) * mm, "mid": v(578.5, 0) * mm, "end": v(579.7, -7.07) * mm});
            skLineSegment(sketch, "E124.6.0.41", {"start": v(585.5, -39.73) * mm, "end": v(581.4, -24.48) * mm});
            skLineSegment(sketch, "E124.6.0.42", {"start": v(556.57, 10.67) * mm, "end": v(575.74, 15.8) * mm});
            skArc(sketch, "E124.6.0.43", {"start": v(645, 39) * mm, "mid": v(643.24, 43.24) * mm, "end": v(639, 45) * mm});
            skArc(sketch, "E124.6.0.44", {"start": v(591.14, -23.09) * mm, "mid": v(600, -25) * mm, "end": v(608.86, -23.09) * mm});
            skLineSegment(sketch, "E124.6.0.45", {"start": v(583.56, 42.25) * mm, "end": v(561, 42.25) * mm});
            skLineSegment(sketch, "E124.6.0.46", {"start": v(611.88, -45) * mm, "end": v(639, -45) * mm});
            skLineSegment(sketch, "E124.6.0.47", {"start": v(645, -39) * mm, "end": v(645, 39) * mm});
            skLineSegment(sketch, "E124.6.0.48", {"start": v(577, 14.84) * mm, "end": v(577, 9.27) * mm});
            skArc(sketch, "E124.6.0.49", {"start": v(557.75, 16.44) * mm, "mid": v(558.53, 14.85) * mm, "end": v(560.27, 14.5) * mm});
            skLineSegment(sketch, "E124.6.0.50", {"start": v(619.25, 20.25) * mm, "end": v(607.4, 20.25) * mm});
            skArc(sketch, "E124.6.0.51", {"start": v(614.84, 23) * mm, "mid": v(615.64, 23.4) * mm, "end": v(615.8, 24.26) * mm});
            skArc(sketch, "E124.6.0.52", {"start": v(584.2, 24.26) * mm, "mid": v(584.36, 23.4) * mm, "end": v(585.16, 23) * mm});
            skArc(sketch, "E124.6.0.53", {"start": v(556.57, -10.67) * mm, "mid": v(555.49, -10.89) * mm, "end": v(555, -11.88) * mm});
            skArc(sketch, "E124.6.0.54", {"start": v(577, 14.84) * mm, "mid": v(576.6, 15.64) * mm, "end": v(575.74, 15.8) * mm});
            skArc(sketch, "E124.6.0.55", {"start": v(585.5, 39.73) * mm, "mid": v(585.15, 41.47) * mm, "end": v(583.56, 42.25) * mm});
            skArc(sketch, "E124.6.0.56", {"start": v(639, -42.25) * mm, "mid": v(641.3, -41.3) * mm, "end": v(642.25, -39) * mm});
            skLineSegment(sketch, "E124.6.0.57", {"start": v(607.4, -20.25) * mm, "end": v(619.25, -20.25) * mm});
            skArc(sketch, "E124.6.0.58", {"start": v(561, 42.25) * mm, "mid": v(558.7, 41.3) * mm, "end": v(557.75, 39) * mm});
            skArc(sketch, "E124.6.0.59", {"start": v(583.56, -42.25) * mm, "mid": v(585.15, -41.47) * mm, "end": v(585.5, -39.73) * mm});
            skLineSegment(sketch, "E124.6.0.60", {"start": v(580.75, -20.25) * mm, "end": v(592.6, -20.25) * mm});
            skArc(sketch, "E124.6.0.61", {"start": v(623, -14.84) * mm, "mid": v(623.4, -15.64) * mm, "end": v(624.26, -15.8) * mm});
            skArc(sketch, "E124.6.0.62", {"start": v(642.25, -16.44) * mm, "mid": v(641.47, -14.85) * mm, "end": v(639.73, -14.5) * mm});
            skLineSegment(sketch, "E124.6.0.63", {"start": v(623, 14.84) * mm, "end": v(623, 9.27) * mm});
            skArc(sketch, "E124.6.0.64", {"start": v(560.27, -14.5) * mm, "mid": v(558.53, -14.85) * mm, "end": v(557.75, -16.44) * mm});
            skArc(sketch, "E124.6.0.65", {"start": v(616.44, 42.25) * mm, "mid": v(614.85, 41.47) * mm, "end": v(614.5, 39.73) * mm});
            skArc(sketch, "E124.6.0.66", {"start": v(610.67, -43.43) * mm, "mid": v(610.89, -44.51) * mm, "end": v(611.88, -45) * mm});
            skArc(sketch, "E124.6.0.67", {"start": v(618.6, 24.48) * mm, "mid": v(619.3, 23.41) * mm, "end": v(620.53, 23) * mm});
            skLineSegment(sketch, "E124.6.0.68", {"start": v(577, -9.27) * mm, "end": v(577, -14.84) * mm});
            skArc(sketch, "E124.6.0.69", {"start": v(575.74, -15.8) * mm, "mid": v(576.6, -15.64) * mm, "end": v(577, -14.84) * mm});
            skLineSegment(sketch, "E124.6.0.70", {"start": v(623, -9.27) * mm, "end": v(623, -14.84) * mm});
            skLineSegment(sketch, "E124.6.0.71", {"start": v(609.27, 23) * mm, "end": v(614.84, 23) * mm});
            skArc(sketch, "E124.6.0.72", {"start": v(555, 11.88) * mm, "mid": v(555.49, 10.89) * mm, "end": v(556.57, 10.67) * mm});
            skArc(sketch, "E124.6.0.73", {"start": v(639.73, 14.5) * mm, "mid": v(641.47, 14.85) * mm, "end": v(642.25, 16.44) * mm});
            skLineSegment(sketch, "E124.6.0.74", {"start": v(592.6, 20.25) * mm, "end": v(580.75, 20.25) * mm});
            skArc(sketch, "E124.6.0.75", {"start": v(614.5, -39.73) * mm, "mid": v(614.85, -41.47) * mm, "end": v(616.44, -42.25) * mm});
            skLineSegment(sketch, "E124.6.0.76", {"start": v(609.27, -23) * mm, "end": v(614.84, -23) * mm});
            skLineSegment(sketch, "E124.6.0.77", {"start": v(585.16, 23) * mm, "end": v(590.73, 23) * mm});
            skArc(sketch, "E124.6.0.78", {"start": v(620.25, 19.25) * mm, "mid": v(619.96, 19.96) * mm, "end": v(619.25, 20.25) * mm});
            skArc(sketch, "E124.6.0.79", {"start": v(642.25, 39) * mm, "mid": v(641.3, 41.3) * mm, "end": v(639, 42.25) * mm});
            skArc(sketch, "E124.6.0.80", {"start": v(620.53, -23) * mm, "mid": v(619.3, -23.41) * mm, "end": v(618.6, -24.48) * mm});
            skArc(sketch, "E124.6.0.81", {"start": v(579.47, 23) * mm, "mid": v(580.7, 23.41) * mm, "end": v(581.4, 24.48) * mm});
            skArc(sketch, "E124.6.0.82", {"start": v(615.8, -24.26) * mm, "mid": v(615.64, -23.4) * mm, "end": v(614.84, -23) * mm});
            skArc(sketch, "E124.6.0.83", {"start": v(585.16, -23) * mm, "mid": v(584.36, -23.4) * mm, "end": v(584.2, -24.26) * mm});
            skArc(sketch, "E124.6.0.84", {"start": v(619.25, -20.25) * mm, "mid": v(619.96, -19.96) * mm, "end": v(620.25, -19.25) * mm});
            skArc(sketch, "E124.6.0.85", {"start": v(579.75, -19.25) * mm, "mid": v(580.04, -19.96) * mm, "end": v(580.75, -20.25) * mm});
            skArc(sketch, "E124.6.0.86", {"start": v(580.75, 20.25) * mm, "mid": v(580.04, 19.96) * mm, "end": v(579.75, 19.25) * mm});
            skArc(sketch, "E124.6.0.87", {"start": v(588.12, -45) * mm, "mid": v(589.11, -44.51) * mm, "end": v(589.33, -43.43) * mm});
            skLineSegment(sketch, "E124.6.0.88", {"start": v(585.16, -23) * mm, "end": v(590.73, -23) * mm});
            skArc(sketch, "E124.6.0.89", {"start": v(581.4, -24.48) * mm, "mid": v(580.7, -23.41) * mm, "end": v(579.47, -23) * mm});
            skArc(sketch, "E124.6.0.90", {"start": v(557.75, -39) * mm, "mid": v(558.7, -41.3) * mm, "end": v(561, -42.25) * mm});
            skArc(sketch, "E124.6.0.91", {"start": v(624.26, 15.8) * mm, "mid": v(623.4, 15.64) * mm, "end": v(623, 14.84) * mm});
            skArc(sketch, "E124.6.0.92", {"start": v(623.09, -8.86) * mm, "mid": v(623.02, -9.06) * mm, "end": v(623, -9.27) * mm});
            skArc(sketch, "E124.6.0.93", {"start": v(577, -20.53) * mm, "mid": v(576.59, -19.3) * mm, "end": v(575.52, -18.6) * mm});
            skArc(sketch, "E124.6.0.94", {"start": v(577, -21) * mm, "mid": v(577.59, -22.41) * mm, "end": v(579, -23) * mm});
            skLineSegment(sketch, "E124.6.0.95", {"start": v(579, 23) * mm, "end": v(579.47, 23) * mm});
            skArc(sketch, "E124.6.0.96", {"start": v(608.86, 23.09) * mm, "mid": v(609.06, 23.02) * mm, "end": v(609.27, 23) * mm});
            skArc(sketch, "E124.6.0.97", {"start": v(623, 9.27) * mm, "mid": v(623.02, 9.06) * mm, "end": v(623.09, 8.86) * mm});
            skArc(sketch, "E124.6.0.98", {"start": v(620.25, 7.4) * mm, "mid": v(620.26, 7.23) * mm, "end": v(620.3, 7.07) * mm});
            skArc(sketch, "E124.6.0.99", {"start": v(579, 23) * mm, "mid": v(577.59, 22.41) * mm, "end": v(577, 21) * mm});
            skArc(sketch, "E124.6.0.100", {"start": v(579.75, -7.4) * mm, "mid": v(579.74, -7.23) * mm, "end": v(579.7, -7.07) * mm});
            skArc(sketch, "E124.6.0.101", {"start": v(576.91, 8.86) * mm, "mid": v(576.98, 9.06) * mm, "end": v(577, 9.27) * mm});
            skArc(sketch, "E124.6.0.102", {"start": v(592.6, 20.25) * mm, "mid": v(592.77, 20.26) * mm, "end": v(592.93, 20.3) * mm});
            skLineSegment(sketch, "E124.6.0.103", {"start": v(579.47, -23) * mm, "end": v(579, -23) * mm});
            skArc(sketch, "E124.6.0.104", {"start": v(620.3, -7.07) * mm, "mid": v(620.26, -7.23) * mm, "end": v(620.25, -7.4) * mm});
            skArc(sketch, "E124.6.0.105", {"start": v(579.7, 7.07) * mm, "mid": v(579.74, 7.23) * mm, "end": v(579.75, 7.4) * mm});
            skArc(sketch, "E124.6.0.106", {"start": v(590.73, 23) * mm, "mid": v(590.94, 23.02) * mm, "end": v(591.14, 23.09) * mm});
            skLineSegment(sketch, "E124.6.0.107", {"start": v(577, -21) * mm, "end": v(577, -20.53) * mm});
            skArc(sketch, "E124.6.0.108", {"start": v(575.52, 18.6) * mm, "mid": v(576.59, 19.3) * mm, "end": v(577, 20.53) * mm});
            skArc(sketch, "E124.6.0.109", {"start": v(577, -9.27) * mm, "mid": v(576.98, -9.06) * mm, "end": v(576.91, -8.86) * mm});
            skArc(sketch, "E124.6.0.110", {"start": v(607.07, 20.3) * mm, "mid": v(607.23, 20.26) * mm, "end": v(607.4, 20.25) * mm});
            skLineSegment(sketch, "E124.6.0.111", {"start": v(620.53, 23) * mm, "end": v(621, 23) * mm});
            skArc(sketch, "E124.6.0.112", {"start": v(624.48, -18.6) * mm, "mid": v(623.41, -19.3) * mm, "end": v(623, -20.53) * mm});
            skArc(sketch, "E124.6.0.113", {"start": v(607.4, -20.25) * mm, "mid": v(607.23, -20.26) * mm, "end": v(607.07, -20.3) * mm});
            skArc(sketch, "E124.6.0.114", {"start": v(621, -23) * mm, "mid": v(622.41, -22.41) * mm, "end": v(623, -21) * mm});
            skLineSegment(sketch, "E124.6.0.115", {"start": v(621, -23) * mm, "end": v(620.53, -23) * mm});
            skLineSegment(sketch, "E124.6.0.116", {"start": v(623, -20.53) * mm, "end": v(623, -21) * mm});
            skArc(sketch, "E124.6.0.117", {"start": v(609.27, -23) * mm, "mid": v(609.06, -23.02) * mm, "end": v(608.86, -23.09) * mm});
            skArc(sketch, "E124.6.0.118", {"start": v(591.14, -23.09) * mm, "mid": v(590.94, -23.02) * mm, "end": v(590.73, -23) * mm});
            skArc(sketch, "E124.6.0.119", {"start": v(623, 20.53) * mm, "mid": v(623.41, 19.3) * mm, "end": v(624.48, 18.6) * mm});
            skArc(sketch, "E124.6.0.120", {"start": v(592.93, -20.3) * mm, "mid": v(592.77, -20.26) * mm, "end": v(592.6, -20.25) * mm});
            skLineSegment(sketch, "E124.6.0.121", {"start": v(577, 20.53) * mm, "end": v(577, 21) * mm});
            skArc(sketch, "E124.6.0.122", {"start": v(623, 21) * mm, "mid": v(622.41, 22.41) * mm, "end": v(621, 23) * mm});
            skLineSegment(sketch, "E124.6.0.123", {"start": v(623, 21) * mm, "end": v(623, 20.53) * mm});
            skLineSegment(sketch, "E124.7.0.0", {"start": v(657.75, 39) * mm, "end": v(657.75, 16.44) * mm});
            skLineSegment(sketch, "E124.7.0.1", {"start": v(715.8, 24.26) * mm, "end": v(710.99, 42.25) * mm});
            skLineSegment(sketch, "E124.7.0.2", {"start": v(689.01, 42.25) * mm, "end": v(684.2, 24.26) * mm});
            skArc(sketch, "E124.7.0.3", {"start": v(707.07, 20.3) * mm, "mid": v(700, 21.5) * mm, "end": v(692.93, 20.3) * mm});
            skLineSegment(sketch, "E124.7.0.4", {"start": v(660.27, 14.5) * mm, "end": v(675.52, 18.6) * mm});
            skLineSegment(sketch, "E124.7.0.5", {"start": v(681.4, 24.48) * mm, "end": v(685.5, 39.73) * mm});
            skLineSegment(sketch, "E124.7.0.6", {"start": v(739, 45) * mm, "end": v(661, 45) * mm});
            skArc(sketch, "E124.7.0.7", {"start": v(739, -45) * mm, "mid": v(743.24, -43.24) * mm, "end": v(745, -39) * mm});
            skArc(sketch, "E124.7.0.8", {"start": v(692.93, -20.3) * mm, "mid": v(700, -21.5) * mm, "end": v(707.07, -20.3) * mm});
            skLineSegment(sketch, "E124.7.0.9", {"start": v(720.25, -19.25) * mm, "end": v(720.25, -7.4) * mm});
            skLineSegment(sketch, "E124.7.0.10", {"start": v(679.75, 19.25) * mm, "end": v(679.75, 7.4) * mm});
            skLineSegment(sketch, "E124.7.0.11", {"start": v(718.6, -24.48) * mm, "end": v(714.5, -39.73) * mm});
            skArc(sketch, "E124.7.0.12", {"start": v(676.91, 8.86) * mm, "mid": v(675, 0) * mm, "end": v(676.91, -8.86) * mm});
            skLineSegment(sketch, "E124.7.0.13", {"start": v(714.5, 39.73) * mm, "end": v(718.6, 24.48) * mm});
            skLineSegment(sketch, "E124.7.0.14", {"start": v(716.44, -42.25) * mm, "end": v(739, -42.25) * mm});
            skLineSegment(sketch, "E124.7.0.15", {"start": v(710.99, 42.25) * mm, "end": v(689.01, 42.25) * mm});
            skLineSegment(sketch, "E124.7.0.16", {"start": v(655, 39) * mm, "end": v(655, 11.88) * mm});
            skLineSegment(sketch, "E124.7.0.17", {"start": v(720.25, 7.4) * mm, "end": v(720.25, 19.25) * mm});
            skLineSegment(sketch, "E124.7.0.18", {"start": v(655, -11.88) * mm, "end": v(655, -39) * mm});
            skLineSegment(sketch, "E124.7.0.19", {"start": v(742.25, -39) * mm, "end": v(742.25, -16.44) * mm});
            skLineSegment(sketch, "E124.7.0.20", {"start": v(657.75, -16.44) * mm, "end": v(657.75, -39) * mm});
            skArc(sketch, "E124.7.0.21", {"start": v(661, 45) * mm, "mid": v(656.76, 43.24) * mm, "end": v(655, 39) * mm});
            skArc(sketch, "E124.7.0.22", {"start": v(723.09, -8.86) * mm, "mid": v(725, 0) * mm, "end": v(723.09, 8.86) * mm});
            skArc(sketch, "E124.7.0.23", {"start": v(708.86, 23.09) * mm, "mid": v(700, 25) * mm, "end": v(691.14, 23.09) * mm});
            skLineSegment(sketch, "E124.7.0.24", {"start": v(742.25, 16.44) * mm, "end": v(742.25, 39) * mm});
            skArc(sketch, "E124.7.0.25", {"start": v(655, -39) * mm, "mid": v(656.76, -43.24) * mm, "end": v(661, -45) * mm});
            skArc(sketch, "E124.7.0.26", {"start": v(720.3, -7.07) * mm, "mid": v(721.5, 0) * mm, "end": v(720.3, 7.07) * mm});
            skLineSegment(sketch, "E124.7.0.27", {"start": v(742.25, -10.99) * mm, "end": v(742.25, 10.99) * mm});
            skLineSegment(sketch, "E124.7.0.28", {"start": v(739.73, -14.5) * mm, "end": v(724.48, -18.6) * mm});
            skLineSegment(sketch, "E124.7.0.29", {"start": v(679.75, -7.4) * mm, "end": v(679.75, -19.25) * mm});
            skLineSegment(sketch, "E124.7.0.30", {"start": v(724.48, 18.6) * mm, "end": v(739.73, 14.5) * mm});
            skLineSegment(sketch, "E124.7.0.31", {"start": v(675.74, -15.8) * mm, "end": v(656.57, -10.67) * mm});
            skLineSegment(sketch, "E124.7.0.32", {"start": v(739, 42.25) * mm, "end": v(716.44, 42.25) * mm});
            skLineSegment(sketch, "E124.7.0.33", {"start": v(724.26, -15.8) * mm, "end": v(742.25, -10.99) * mm});
            skLineSegment(sketch, "E124.7.0.34", {"start": v(689.33, -43.43) * mm, "end": v(684.2, -24.26) * mm});
            skLineSegment(sketch, "E124.7.0.35", {"start": v(675.52, -18.6) * mm, "end": v(660.27, -14.5) * mm});
            skLineSegment(sketch, "E124.7.0.36", {"start": v(661, -42.25) * mm, "end": v(683.56, -42.25) * mm});
            skLineSegment(sketch, "E124.7.0.37", {"start": v(715.8, -24.26) * mm, "end": v(710.67, -43.43) * mm});
            skLineSegment(sketch, "E124.7.0.38", {"start": v(661, -45) * mm, "end": v(688.12, -45) * mm});
            skLineSegment(sketch, "E124.7.0.39", {"start": v(742.25, 10.99) * mm, "end": v(724.26, 15.8) * mm});
            skArc(sketch, "E124.7.0.40", {"start": v(679.7, 7.07) * mm, "mid": v(678.5, 0) * mm, "end": v(679.7, -7.07) * mm});
            skLineSegment(sketch, "E124.7.0.41", {"start": v(685.5, -39.73) * mm, "end": v(681.4, -24.48) * mm});
            skLineSegment(sketch, "E124.7.0.42", {"start": v(656.57, 10.67) * mm, "end": v(675.74, 15.8) * mm});
            skArc(sketch, "E124.7.0.43", {"start": v(745, 39) * mm, "mid": v(743.24, 43.24) * mm, "end": v(739, 45) * mm});
            skArc(sketch, "E124.7.0.44", {"start": v(691.14, -23.09) * mm, "mid": v(700, -25) * mm, "end": v(708.86, -23.09) * mm});
            skLineSegment(sketch, "E124.7.0.45", {"start": v(683.56, 42.25) * mm, "end": v(661, 42.25) * mm});
            skLineSegment(sketch, "E124.7.0.46", {"start": v(711.88, -45) * mm, "end": v(739, -45) * mm});
            skLineSegment(sketch, "E124.7.0.47", {"start": v(745, -39) * mm, "end": v(745, 39) * mm});
            skLineSegment(sketch, "E124.7.0.48", {"start": v(677, 14.84) * mm, "end": v(677, 9.27) * mm});
            skArc(sketch, "E124.7.0.49", {"start": v(657.75, 16.44) * mm, "mid": v(658.53, 14.85) * mm, "end": v(660.27, 14.5) * mm});
            skLineSegment(sketch, "E124.7.0.50", {"start": v(719.25, 20.25) * mm, "end": v(707.4, 20.25) * mm});
            skArc(sketch, "E124.7.0.51", {"start": v(714.84, 23) * mm, "mid": v(715.64, 23.4) * mm, "end": v(715.8, 24.26) * mm});
            skArc(sketch, "E124.7.0.52", {"start": v(684.2, 24.26) * mm, "mid": v(684.36, 23.4) * mm, "end": v(685.16, 23) * mm});
            skArc(sketch, "E124.7.0.53", {"start": v(656.57, -10.67) * mm, "mid": v(655.49, -10.89) * mm, "end": v(655, -11.88) * mm});
            skArc(sketch, "E124.7.0.54", {"start": v(677, 14.84) * mm, "mid": v(676.6, 15.64) * mm, "end": v(675.74, 15.8) * mm});
            skArc(sketch, "E124.7.0.55", {"start": v(685.5, 39.73) * mm, "mid": v(685.15, 41.47) * mm, "end": v(683.56, 42.25) * mm});
            skArc(sketch, "E124.7.0.56", {"start": v(739, -42.25) * mm, "mid": v(741.3, -41.3) * mm, "end": v(742.25, -39) * mm});
            skLineSegment(sketch, "E124.7.0.57", {"start": v(707.4, -20.25) * mm, "end": v(719.25, -20.25) * mm});
            skArc(sketch, "E124.7.0.58", {"start": v(661, 42.25) * mm, "mid": v(658.7, 41.3) * mm, "end": v(657.75, 39) * mm});
            skArc(sketch, "E124.7.0.59", {"start": v(683.56, -42.25) * mm, "mid": v(685.15, -41.47) * mm, "end": v(685.5, -39.73) * mm});
            skLineSegment(sketch, "E124.7.0.60", {"start": v(680.75, -20.25) * mm, "end": v(692.6, -20.25) * mm});
            skArc(sketch, "E124.7.0.61", {"start": v(723, -14.84) * mm, "mid": v(723.4, -15.64) * mm, "end": v(724.26, -15.8) * mm});
            skArc(sketch, "E124.7.0.62", {"start": v(742.25, -16.44) * mm, "mid": v(741.47, -14.85) * mm, "end": v(739.73, -14.5) * mm});
            skLineSegment(sketch, "E124.7.0.63", {"start": v(723, 14.84) * mm, "end": v(723, 9.27) * mm});
            skArc(sketch, "E124.7.0.64", {"start": v(660.27, -14.5) * mm, "mid": v(658.53, -14.85) * mm, "end": v(657.75, -16.44) * mm});
            skArc(sketch, "E124.7.0.65", {"start": v(716.44, 42.25) * mm, "mid": v(714.85, 41.47) * mm, "end": v(714.5, 39.73) * mm});
            skArc(sketch, "E124.7.0.66", {"start": v(710.67, -43.43) * mm, "mid": v(710.89, -44.51) * mm, "end": v(711.88, -45) * mm});
            skArc(sketch, "E124.7.0.67", {"start": v(718.6, 24.48) * mm, "mid": v(719.3, 23.41) * mm, "end": v(720.53, 23) * mm});
            skLineSegment(sketch, "E124.7.0.68", {"start": v(677, -9.27) * mm, "end": v(677, -14.84) * mm});
            skArc(sketch, "E124.7.0.69", {"start": v(675.74, -15.8) * mm, "mid": v(676.6, -15.64) * mm, "end": v(677, -14.84) * mm});
            skLineSegment(sketch, "E124.7.0.70", {"start": v(723, -9.27) * mm, "end": v(723, -14.84) * mm});
            skLineSegment(sketch, "E124.7.0.71", {"start": v(709.27, 23) * mm, "end": v(714.84, 23) * mm});
            skArc(sketch, "E124.7.0.72", {"start": v(655, 11.88) * mm, "mid": v(655.49, 10.89) * mm, "end": v(656.57, 10.67) * mm});
            skArc(sketch, "E124.7.0.73", {"start": v(739.73, 14.5) * mm, "mid": v(741.47, 14.85) * mm, "end": v(742.25, 16.44) * mm});
            skLineSegment(sketch, "E124.7.0.74", {"start": v(692.6, 20.25) * mm, "end": v(680.75, 20.25) * mm});
            skArc(sketch, "E124.7.0.75", {"start": v(714.5, -39.73) * mm, "mid": v(714.85, -41.47) * mm, "end": v(716.44, -42.25) * mm});
            skLineSegment(sketch, "E124.7.0.76", {"start": v(709.27, -23) * mm, "end": v(714.84, -23) * mm});
            skLineSegment(sketch, "E124.7.0.77", {"start": v(685.16, 23) * mm, "end": v(690.73, 23) * mm});
            skArc(sketch, "E124.7.0.78", {"start": v(720.25, 19.25) * mm, "mid": v(719.96, 19.96) * mm, "end": v(719.25, 20.25) * mm});
            skArc(sketch, "E124.7.0.79", {"start": v(742.25, 39) * mm, "mid": v(741.3, 41.3) * mm, "end": v(739, 42.25) * mm});
            skArc(sketch, "E124.7.0.80", {"start": v(720.53, -23) * mm, "mid": v(719.3, -23.41) * mm, "end": v(718.6, -24.48) * mm});
            skArc(sketch, "E124.7.0.81", {"start": v(679.47, 23) * mm, "mid": v(680.7, 23.41) * mm, "end": v(681.4, 24.48) * mm});
            skArc(sketch, "E124.7.0.82", {"start": v(715.8, -24.26) * mm, "mid": v(715.64, -23.4) * mm, "end": v(714.84, -23) * mm});
            skArc(sketch, "E124.7.0.83", {"start": v(685.16, -23) * mm, "mid": v(684.36, -23.4) * mm, "end": v(684.2, -24.26) * mm});
            skArc(sketch, "E124.7.0.84", {"start": v(719.25, -20.25) * mm, "mid": v(719.96, -19.96) * mm, "end": v(720.25, -19.25) * mm});
            skArc(sketch, "E124.7.0.85", {"start": v(679.75, -19.25) * mm, "mid": v(680.04, -19.96) * mm, "end": v(680.75, -20.25) * mm});
            skArc(sketch, "E124.7.0.86", {"start": v(680.75, 20.25) * mm, "mid": v(680.04, 19.96) * mm, "end": v(679.75, 19.25) * mm});
            skArc(sketch, "E124.7.0.87", {"start": v(688.12, -45) * mm, "mid": v(689.11, -44.51) * mm, "end": v(689.33, -43.43) * mm});
            skLineSegment(sketch, "E124.7.0.88", {"start": v(685.16, -23) * mm, "end": v(690.73, -23) * mm});
            skArc(sketch, "E124.7.0.89", {"start": v(681.4, -24.48) * mm, "mid": v(680.7, -23.41) * mm, "end": v(679.47, -23) * mm});
            skArc(sketch, "E124.7.0.90", {"start": v(657.75, -39) * mm, "mid": v(658.7, -41.3) * mm, "end": v(661, -42.25) * mm});
            skArc(sketch, "E124.7.0.91", {"start": v(724.26, 15.8) * mm, "mid": v(723.4, 15.64) * mm, "end": v(723, 14.84) * mm});
            skArc(sketch, "E124.7.0.92", {"start": v(723.09, -8.86) * mm, "mid": v(723.02, -9.06) * mm, "end": v(723, -9.27) * mm});
            skArc(sketch, "E124.7.0.93", {"start": v(677, -20.53) * mm, "mid": v(676.59, -19.3) * mm, "end": v(675.52, -18.6) * mm});
            skArc(sketch, "E124.7.0.94", {"start": v(677, -21) * mm, "mid": v(677.59, -22.41) * mm, "end": v(679, -23) * mm});
            skLineSegment(sketch, "E124.7.0.95", {"start": v(679, 23) * mm, "end": v(679.47, 23) * mm});
            skArc(sketch, "E124.7.0.96", {"start": v(708.86, 23.09) * mm, "mid": v(709.06, 23.02) * mm, "end": v(709.27, 23) * mm});
            skArc(sketch, "E124.7.0.97", {"start": v(723, 9.27) * mm, "mid": v(723.02, 9.06) * mm, "end": v(723.09, 8.86) * mm});
            skArc(sketch, "E124.7.0.98", {"start": v(720.25, 7.4) * mm, "mid": v(720.26, 7.23) * mm, "end": v(720.3, 7.07) * mm});
            skArc(sketch, "E124.7.0.99", {"start": v(679, 23) * mm, "mid": v(677.59, 22.41) * mm, "end": v(677, 21) * mm});
            skArc(sketch, "E124.7.0.100", {"start": v(679.75, -7.4) * mm, "mid": v(679.74, -7.23) * mm, "end": v(679.7, -7.07) * mm});
            skArc(sketch, "E124.7.0.101", {"start": v(676.91, 8.86) * mm, "mid": v(676.98, 9.06) * mm, "end": v(677, 9.27) * mm});
            skArc(sketch, "E124.7.0.102", {"start": v(692.6, 20.25) * mm, "mid": v(692.77, 20.26) * mm, "end": v(692.93, 20.3) * mm});
            skLineSegment(sketch, "E124.7.0.103", {"start": v(679.47, -23) * mm, "end": v(679, -23) * mm});
            skArc(sketch, "E124.7.0.104", {"start": v(720.3, -7.07) * mm, "mid": v(720.26, -7.23) * mm, "end": v(720.25, -7.4) * mm});
            skArc(sketch, "E124.7.0.105", {"start": v(679.7, 7.07) * mm, "mid": v(679.74, 7.23) * mm, "end": v(679.75, 7.4) * mm});
            skArc(sketch, "E124.7.0.106", {"start": v(690.73, 23) * mm, "mid": v(690.94, 23.02) * mm, "end": v(691.14, 23.09) * mm});
            skLineSegment(sketch, "E124.7.0.107", {"start": v(677, -21) * mm, "end": v(677, -20.53) * mm});
            skArc(sketch, "E124.7.0.108", {"start": v(675.52, 18.6) * mm, "mid": v(676.59, 19.3) * mm, "end": v(677, 20.53) * mm});
            skArc(sketch, "E124.7.0.109", {"start": v(677, -9.27) * mm, "mid": v(676.98, -9.06) * mm, "end": v(676.91, -8.86) * mm});
            skArc(sketch, "E124.7.0.110", {"start": v(707.07, 20.3) * mm, "mid": v(707.23, 20.26) * mm, "end": v(707.4, 20.25) * mm});
            skLineSegment(sketch, "E124.7.0.111", {"start": v(720.53, 23) * mm, "end": v(721, 23) * mm});
            skArc(sketch, "E124.7.0.112", {"start": v(724.48, -18.6) * mm, "mid": v(723.41, -19.3) * mm, "end": v(723, -20.53) * mm});
            skArc(sketch, "E124.7.0.113", {"start": v(707.4, -20.25) * mm, "mid": v(707.23, -20.26) * mm, "end": v(707.07, -20.3) * mm});
            skArc(sketch, "E124.7.0.114", {"start": v(721, -23) * mm, "mid": v(722.41, -22.41) * mm, "end": v(723, -21) * mm});
            skLineSegment(sketch, "E124.7.0.115", {"start": v(721, -23) * mm, "end": v(720.53, -23) * mm});
            skLineSegment(sketch, "E124.7.0.116", {"start": v(723, -20.53) * mm, "end": v(723, -21) * mm});
            skArc(sketch, "E124.7.0.117", {"start": v(709.27, -23) * mm, "mid": v(709.06, -23.02) * mm, "end": v(708.86, -23.09) * mm});
            skArc(sketch, "E124.7.0.118", {"start": v(691.14, -23.09) * mm, "mid": v(690.94, -23.02) * mm, "end": v(690.73, -23) * mm});
            skArc(sketch, "E124.7.0.119", {"start": v(723, 20.53) * mm, "mid": v(723.41, 19.3) * mm, "end": v(724.48, 18.6) * mm});
            skArc(sketch, "E124.7.0.120", {"start": v(692.93, -20.3) * mm, "mid": v(692.77, -20.26) * mm, "end": v(692.6, -20.25) * mm});
            skLineSegment(sketch, "E124.7.0.121", {"start": v(677, 20.53) * mm, "end": v(677, 21) * mm});
            skArc(sketch, "E124.7.0.122", {"start": v(723, 21) * mm, "mid": v(722.41, 22.41) * mm, "end": v(721, 23) * mm});
            skLineSegment(sketch, "E124.7.0.123", {"start": v(723, 21) * mm, "end": v(723, 20.53) * mm});
            skLineSegment(sketch, "E124.8.0.0", {"start": v(757.75, 39) * mm, "end": v(757.75, 16.44) * mm});
            skLineSegment(sketch, "E124.8.0.1", {"start": v(815.8, 24.26) * mm, "end": v(810.99, 42.25) * mm});
            skLineSegment(sketch, "E124.8.0.2", {"start": v(789.01, 42.25) * mm, "end": v(784.2, 24.26) * mm});
            skArc(sketch, "E124.8.0.3", {"start": v(807.07, 20.3) * mm, "mid": v(800, 21.5) * mm, "end": v(792.93, 20.3) * mm});
            skLineSegment(sketch, "E124.8.0.4", {"start": v(760.27, 14.5) * mm, "end": v(775.52, 18.6) * mm});
            skLineSegment(sketch, "E124.8.0.5", {"start": v(781.4, 24.48) * mm, "end": v(785.5, 39.73) * mm});
            skLineSegment(sketch, "E124.8.0.6", {"start": v(839, 45) * mm, "end": v(761, 45) * mm});
            skArc(sketch, "E124.8.0.7", {"start": v(839, -45) * mm, "mid": v(843.24, -43.24) * mm, "end": v(845, -39) * mm});
            skArc(sketch, "E124.8.0.8", {"start": v(792.93, -20.3) * mm, "mid": v(800, -21.5) * mm, "end": v(807.07, -20.3) * mm});
            skLineSegment(sketch, "E124.8.0.9", {"start": v(820.25, -19.25) * mm, "end": v(820.25, -7.4) * mm});
            skLineSegment(sketch, "E124.8.0.10", {"start": v(779.75, 19.25) * mm, "end": v(779.75, 7.4) * mm});
            skLineSegment(sketch, "E124.8.0.11", {"start": v(818.6, -24.48) * mm, "end": v(814.5, -39.73) * mm});
            skArc(sketch, "E124.8.0.12", {"start": v(776.91, 8.86) * mm, "mid": v(775, 0) * mm, "end": v(776.91, -8.86) * mm});
            skLineSegment(sketch, "E124.8.0.13", {"start": v(814.5, 39.73) * mm, "end": v(818.6, 24.48) * mm});
            skLineSegment(sketch, "E124.8.0.14", {"start": v(816.44, -42.25) * mm, "end": v(839, -42.25) * mm});
            skLineSegment(sketch, "E124.8.0.15", {"start": v(810.99, 42.25) * mm, "end": v(789.01, 42.25) * mm});
            skLineSegment(sketch, "E124.8.0.16", {"start": v(755, 39) * mm, "end": v(755, 11.88) * mm});
            skLineSegment(sketch, "E124.8.0.17", {"start": v(820.25, 7.4) * mm, "end": v(820.25, 19.25) * mm});
            skLineSegment(sketch, "E124.8.0.18", {"start": v(755, -11.88) * mm, "end": v(755, -39) * mm});
            skLineSegment(sketch, "E124.8.0.19", {"start": v(842.25, -39) * mm, "end": v(842.25, -16.44) * mm});
            skLineSegment(sketch, "E124.8.0.20", {"start": v(757.75, -16.44) * mm, "end": v(757.75, -39) * mm});
            skArc(sketch, "E124.8.0.21", {"start": v(761, 45) * mm, "mid": v(756.76, 43.24) * mm, "end": v(755, 39) * mm});
            skArc(sketch, "E124.8.0.22", {"start": v(823.09, -8.86) * mm, "mid": v(825, 0) * mm, "end": v(823.09, 8.86) * mm});
            skArc(sketch, "E124.8.0.23", {"start": v(808.86, 23.09) * mm, "mid": v(800, 25) * mm, "end": v(791.14, 23.09) * mm});
            skLineSegment(sketch, "E124.8.0.24", {"start": v(842.25, 16.44) * mm, "end": v(842.25, 39) * mm});
            skArc(sketch, "E124.8.0.25", {"start": v(755, -39) * mm, "mid": v(756.76, -43.24) * mm, "end": v(761, -45) * mm});
            skArc(sketch, "E124.8.0.26", {"start": v(820.3, -7.07) * mm, "mid": v(821.5, 0) * mm, "end": v(820.3, 7.07) * mm});
            skLineSegment(sketch, "E124.8.0.27", {"start": v(842.25, -10.99) * mm, "end": v(842.25, 10.99) * mm});
            skLineSegment(sketch, "E124.8.0.28", {"start": v(839.73, -14.5) * mm, "end": v(824.48, -18.6) * mm});
            skLineSegment(sketch, "E124.8.0.29", {"start": v(779.75, -7.4) * mm, "end": v(779.75, -19.25) * mm});
            skLineSegment(sketch, "E124.8.0.30", {"start": v(824.48, 18.6) * mm, "end": v(839.73, 14.5) * mm});
            skLineSegment(sketch, "E124.8.0.31", {"start": v(775.74, -15.8) * mm, "end": v(756.57, -10.67) * mm});
            skLineSegment(sketch, "E124.8.0.32", {"start": v(839, 42.25) * mm, "end": v(816.44, 42.25) * mm});
            skLineSegment(sketch, "E124.8.0.33", {"start": v(824.26, -15.8) * mm, "end": v(842.25, -10.99) * mm});
            skLineSegment(sketch, "E124.8.0.34", {"start": v(789.33, -43.43) * mm, "end": v(784.2, -24.26) * mm});
            skLineSegment(sketch, "E124.8.0.35", {"start": v(775.52, -18.6) * mm, "end": v(760.27, -14.5) * mm});
            skLineSegment(sketch, "E124.8.0.36", {"start": v(761, -42.25) * mm, "end": v(783.56, -42.25) * mm});
            skLineSegment(sketch, "E124.8.0.37", {"start": v(815.8, -24.26) * mm, "end": v(810.67, -43.43) * mm});
            skLineSegment(sketch, "E124.8.0.38", {"start": v(761, -45) * mm, "end": v(788.12, -45) * mm});
            skLineSegment(sketch, "E124.8.0.39", {"start": v(842.25, 10.99) * mm, "end": v(824.26, 15.8) * mm});
            skArc(sketch, "E124.8.0.40", {"start": v(779.7, 7.07) * mm, "mid": v(778.5, 0) * mm, "end": v(779.7, -7.07) * mm});
            skLineSegment(sketch, "E124.8.0.41", {"start": v(785.5, -39.73) * mm, "end": v(781.4, -24.48) * mm});
            skLineSegment(sketch, "E124.8.0.42", {"start": v(756.57, 10.67) * mm, "end": v(775.74, 15.8) * mm});
            skArc(sketch, "E124.8.0.43", {"start": v(845, 39) * mm, "mid": v(843.24, 43.24) * mm, "end": v(839, 45) * mm});
            skArc(sketch, "E124.8.0.44", {"start": v(791.14, -23.09) * mm, "mid": v(800, -25) * mm, "end": v(808.86, -23.09) * mm});
            skLineSegment(sketch, "E124.8.0.45", {"start": v(783.56, 42.25) * mm, "end": v(761, 42.25) * mm});
            skLineSegment(sketch, "E124.8.0.46", {"start": v(811.88, -45) * mm, "end": v(839, -45) * mm});
            skLineSegment(sketch, "E124.8.0.47", {"start": v(845, -39) * mm, "end": v(845, 39) * mm});
            skLineSegment(sketch, "E124.8.0.48", {"start": v(777, 14.84) * mm, "end": v(777, 9.27) * mm});
            skArc(sketch, "E124.8.0.49", {"start": v(757.75, 16.44) * mm, "mid": v(758.53, 14.85) * mm, "end": v(760.27, 14.5) * mm});
            skLineSegment(sketch, "E124.8.0.50", {"start": v(819.25, 20.25) * mm, "end": v(807.4, 20.25) * mm});
            skArc(sketch, "E124.8.0.51", {"start": v(814.84, 23) * mm, "mid": v(815.64, 23.4) * mm, "end": v(815.8, 24.26) * mm});
            skArc(sketch, "E124.8.0.52", {"start": v(784.2, 24.26) * mm, "mid": v(784.36, 23.4) * mm, "end": v(785.16, 23) * mm});
            skArc(sketch, "E124.8.0.53", {"start": v(756.57, -10.67) * mm, "mid": v(755.49, -10.89) * mm, "end": v(755, -11.88) * mm});
            skArc(sketch, "E124.8.0.54", {"start": v(777, 14.84) * mm, "mid": v(776.6, 15.64) * mm, "end": v(775.74, 15.8) * mm});
            skArc(sketch, "E124.8.0.55", {"start": v(785.5, 39.73) * mm, "mid": v(785.15, 41.47) * mm, "end": v(783.56, 42.25) * mm});
            skArc(sketch, "E124.8.0.56", {"start": v(839, -42.25) * mm, "mid": v(841.3, -41.3) * mm, "end": v(842.25, -39) * mm});
            skLineSegment(sketch, "E124.8.0.57", {"start": v(807.4, -20.25) * mm, "end": v(819.25, -20.25) * mm});
            skArc(sketch, "E124.8.0.58", {"start": v(761, 42.25) * mm, "mid": v(758.7, 41.3) * mm, "end": v(757.75, 39) * mm});
            skArc(sketch, "E124.8.0.59", {"start": v(783.56, -42.25) * mm, "mid": v(785.15, -41.47) * mm, "end": v(785.5, -39.73) * mm});
            skLineSegment(sketch, "E124.8.0.60", {"start": v(780.75, -20.25) * mm, "end": v(792.6, -20.25) * mm});
            skArc(sketch, "E124.8.0.61", {"start": v(823, -14.84) * mm, "mid": v(823.4, -15.64) * mm, "end": v(824.26, -15.8) * mm});
            skArc(sketch, "E124.8.0.62", {"start": v(842.25, -16.44) * mm, "mid": v(841.47, -14.85) * mm, "end": v(839.73, -14.5) * mm});
            skLineSegment(sketch, "E124.8.0.63", {"start": v(823, 14.84) * mm, "end": v(823, 9.27) * mm});
            skArc(sketch, "E124.8.0.64", {"start": v(760.27, -14.5) * mm, "mid": v(758.53, -14.85) * mm, "end": v(757.75, -16.44) * mm});
            skArc(sketch, "E124.8.0.65", {"start": v(816.44, 42.25) * mm, "mid": v(814.85, 41.47) * mm, "end": v(814.5, 39.73) * mm});
            skArc(sketch, "E124.8.0.66", {"start": v(810.67, -43.43) * mm, "mid": v(810.89, -44.51) * mm, "end": v(811.88, -45) * mm});
            skArc(sketch, "E124.8.0.67", {"start": v(818.6, 24.48) * mm, "mid": v(819.3, 23.41) * mm, "end": v(820.53, 23) * mm});
            skLineSegment(sketch, "E124.8.0.68", {"start": v(777, -9.27) * mm, "end": v(777, -14.84) * mm});
            skArc(sketch, "E124.8.0.69", {"start": v(775.74, -15.8) * mm, "mid": v(776.6, -15.64) * mm, "end": v(777, -14.84) * mm});
            skLineSegment(sketch, "E124.8.0.70", {"start": v(823, -9.27) * mm, "end": v(823, -14.84) * mm});
            skLineSegment(sketch, "E124.8.0.71", {"start": v(809.27, 23) * mm, "end": v(814.84, 23) * mm});
            skArc(sketch, "E124.8.0.72", {"start": v(755, 11.88) * mm, "mid": v(755.49, 10.89) * mm, "end": v(756.57, 10.67) * mm});
            skArc(sketch, "E124.8.0.73", {"start": v(839.73, 14.5) * mm, "mid": v(841.47, 14.85) * mm, "end": v(842.25, 16.44) * mm});
            skLineSegment(sketch, "E124.8.0.74", {"start": v(792.6, 20.25) * mm, "end": v(780.75, 20.25) * mm});
            skArc(sketch, "E124.8.0.75", {"start": v(814.5, -39.73) * mm, "mid": v(814.85, -41.47) * mm, "end": v(816.44, -42.25) * mm});
            skLineSegment(sketch, "E124.8.0.76", {"start": v(809.27, -23) * mm, "end": v(814.84, -23) * mm});
            skLineSegment(sketch, "E124.8.0.77", {"start": v(785.16, 23) * mm, "end": v(790.73, 23) * mm});
            skArc(sketch, "E124.8.0.78", {"start": v(820.25, 19.25) * mm, "mid": v(819.96, 19.96) * mm, "end": v(819.25, 20.25) * mm});
            skArc(sketch, "E124.8.0.79", {"start": v(842.25, 39) * mm, "mid": v(841.3, 41.3) * mm, "end": v(839, 42.25) * mm});
            skArc(sketch, "E124.8.0.80", {"start": v(820.53, -23) * mm, "mid": v(819.3, -23.41) * mm, "end": v(818.6, -24.48) * mm});
            skArc(sketch, "E124.8.0.81", {"start": v(779.47, 23) * mm, "mid": v(780.7, 23.41) * mm, "end": v(781.4, 24.48) * mm});
            skArc(sketch, "E124.8.0.82", {"start": v(815.8, -24.26) * mm, "mid": v(815.64, -23.4) * mm, "end": v(814.84, -23) * mm});
            skArc(sketch, "E124.8.0.83", {"start": v(785.16, -23) * mm, "mid": v(784.36, -23.4) * mm, "end": v(784.2, -24.26) * mm});
            skArc(sketch, "E124.8.0.84", {"start": v(819.25, -20.25) * mm, "mid": v(819.96, -19.96) * mm, "end": v(820.25, -19.25) * mm});
            skArc(sketch, "E124.8.0.85", {"start": v(779.75, -19.25) * mm, "mid": v(780.04, -19.96) * mm, "end": v(780.75, -20.25) * mm});
            skArc(sketch, "E124.8.0.86", {"start": v(780.75, 20.25) * mm, "mid": v(780.04, 19.96) * mm, "end": v(779.75, 19.25) * mm});
            skArc(sketch, "E124.8.0.87", {"start": v(788.12, -45) * mm, "mid": v(789.11, -44.51) * mm, "end": v(789.33, -43.43) * mm});
            skLineSegment(sketch, "E124.8.0.88", {"start": v(785.16, -23) * mm, "end": v(790.73, -23) * mm});
            skArc(sketch, "E124.8.0.89", {"start": v(781.4, -24.48) * mm, "mid": v(780.7, -23.41) * mm, "end": v(779.47, -23) * mm});
            skArc(sketch, "E124.8.0.90", {"start": v(757.75, -39) * mm, "mid": v(758.7, -41.3) * mm, "end": v(761, -42.25) * mm});
            skArc(sketch, "E124.8.0.91", {"start": v(824.26, 15.8) * mm, "mid": v(823.4, 15.64) * mm, "end": v(823, 14.84) * mm});
            skArc(sketch, "E124.8.0.92", {"start": v(823.09, -8.86) * mm, "mid": v(823.02, -9.06) * mm, "end": v(823, -9.27) * mm});
            skArc(sketch, "E124.8.0.93", {"start": v(777, -20.53) * mm, "mid": v(776.59, -19.3) * mm, "end": v(775.52, -18.6) * mm});
            skArc(sketch, "E124.8.0.94", {"start": v(777, -21) * mm, "mid": v(777.59, -22.41) * mm, "end": v(779, -23) * mm});
            skLineSegment(sketch, "E124.8.0.95", {"start": v(779, 23) * mm, "end": v(779.47, 23) * mm});
            skArc(sketch, "E124.8.0.96", {"start": v(808.86, 23.09) * mm, "mid": v(809.06, 23.02) * mm, "end": v(809.27, 23) * mm});
            skArc(sketch, "E124.8.0.97", {"start": v(823, 9.27) * mm, "mid": v(823.02, 9.06) * mm, "end": v(823.09, 8.86) * mm});
            skArc(sketch, "E124.8.0.98", {"start": v(820.25, 7.4) * mm, "mid": v(820.26, 7.23) * mm, "end": v(820.3, 7.07) * mm});
            skArc(sketch, "E124.8.0.99", {"start": v(779, 23) * mm, "mid": v(777.59, 22.41) * mm, "end": v(777, 21) * mm});
            skArc(sketch, "E124.8.0.100", {"start": v(779.75, -7.4) * mm, "mid": v(779.74, -7.23) * mm, "end": v(779.7, -7.07) * mm});
            skArc(sketch, "E124.8.0.101", {"start": v(776.91, 8.86) * mm, "mid": v(776.98, 9.06) * mm, "end": v(777, 9.27) * mm});
            skArc(sketch, "E124.8.0.102", {"start": v(792.6, 20.25) * mm, "mid": v(792.77, 20.26) * mm, "end": v(792.93, 20.3) * mm});
            skLineSegment(sketch, "E124.8.0.103", {"start": v(779.47, -23) * mm, "end": v(779, -23) * mm});
            skArc(sketch, "E124.8.0.104", {"start": v(820.3, -7.07) * mm, "mid": v(820.26, -7.23) * mm, "end": v(820.25, -7.4) * mm});
            skArc(sketch, "E124.8.0.105", {"start": v(779.7, 7.07) * mm, "mid": v(779.74, 7.23) * mm, "end": v(779.75, 7.4) * mm});
            skArc(sketch, "E124.8.0.106", {"start": v(790.73, 23) * mm, "mid": v(790.94, 23.02) * mm, "end": v(791.14, 23.09) * mm});
            skLineSegment(sketch, "E124.8.0.107", {"start": v(777, -21) * mm, "end": v(777, -20.53) * mm});
            skArc(sketch, "E124.8.0.108", {"start": v(775.52, 18.6) * mm, "mid": v(776.59, 19.3) * mm, "end": v(777, 20.53) * mm});
            skArc(sketch, "E124.8.0.109", {"start": v(777, -9.27) * mm, "mid": v(776.98, -9.06) * mm, "end": v(776.91, -8.86) * mm});
            skArc(sketch, "E124.8.0.110", {"start": v(807.07, 20.3) * mm, "mid": v(807.23, 20.26) * mm, "end": v(807.4, 20.25) * mm});
            skLineSegment(sketch, "E124.8.0.111", {"start": v(820.53, 23) * mm, "end": v(821, 23) * mm});
            skArc(sketch, "E124.8.0.112", {"start": v(824.48, -18.6) * mm, "mid": v(823.41, -19.3) * mm, "end": v(823, -20.53) * mm});
            skArc(sketch, "E124.8.0.113", {"start": v(807.4, -20.25) * mm, "mid": v(807.23, -20.26) * mm, "end": v(807.07, -20.3) * mm});
            skArc(sketch, "E124.8.0.114", {"start": v(821, -23) * mm, "mid": v(822.41, -22.41) * mm, "end": v(823, -21) * mm});
            skLineSegment(sketch, "E124.8.0.115", {"start": v(821, -23) * mm, "end": v(820.53, -23) * mm});
            skLineSegment(sketch, "E124.8.0.116", {"start": v(823, -20.53) * mm, "end": v(823, -21) * mm});
            skArc(sketch, "E124.8.0.117", {"start": v(809.27, -23) * mm, "mid": v(809.06, -23.02) * mm, "end": v(808.86, -23.09) * mm});
            skArc(sketch, "E124.8.0.118", {"start": v(791.14, -23.09) * mm, "mid": v(790.94, -23.02) * mm, "end": v(790.73, -23) * mm});
            skArc(sketch, "E124.8.0.119", {"start": v(823, 20.53) * mm, "mid": v(823.41, 19.3) * mm, "end": v(824.48, 18.6) * mm});
            skArc(sketch, "E124.8.0.120", {"start": v(792.93, -20.3) * mm, "mid": v(792.77, -20.26) * mm, "end": v(792.6, -20.25) * mm});
            skLineSegment(sketch, "E124.8.0.121", {"start": v(777, 20.53) * mm, "end": v(777, 21) * mm});
            skArc(sketch, "E124.8.0.122", {"start": v(823, 21) * mm, "mid": v(822.41, 22.41) * mm, "end": v(821, 23) * mm});
            skLineSegment(sketch, "E124.8.0.123", {"start": v(823, 21) * mm, "end": v(823, 20.53) * mm});
            skLineSegment(sketch, "E124.9.0.0", {"start": v(857.75, 39) * mm, "end": v(857.75, 16.44) * mm});
            skLineSegment(sketch, "E124.9.0.1", {"start": v(915.8, 24.26) * mm, "end": v(910.99, 42.25) * mm});
            skLineSegment(sketch, "E124.9.0.2", {"start": v(889.01, 42.25) * mm, "end": v(884.2, 24.26) * mm});
            skArc(sketch, "E124.9.0.3", {"start": v(907.07, 20.3) * mm, "mid": v(900, 21.5) * mm, "end": v(892.93, 20.3) * mm});
            skLineSegment(sketch, "E124.9.0.4", {"start": v(860.27, 14.5) * mm, "end": v(875.52, 18.6) * mm});
            skLineSegment(sketch, "E124.9.0.5", {"start": v(881.4, 24.48) * mm, "end": v(885.5, 39.73) * mm});
            skLineSegment(sketch, "E124.9.0.6", {"start": v(939, 45) * mm, "end": v(861, 45) * mm});
            skArc(sketch, "E124.9.0.7", {"start": v(939, -45) * mm, "mid": v(943.24, -43.24) * mm, "end": v(945, -39) * mm});
            skArc(sketch, "E124.9.0.8", {"start": v(892.93, -20.3) * mm, "mid": v(900, -21.5) * mm, "end": v(907.07, -20.3) * mm});
            skLineSegment(sketch, "E124.9.0.9", {"start": v(920.25, -19.25) * mm, "end": v(920.25, -7.4) * mm});
            skLineSegment(sketch, "E124.9.0.10", {"start": v(879.75, 19.25) * mm, "end": v(879.75, 7.4) * mm});
            skLineSegment(sketch, "E124.9.0.11", {"start": v(918.6, -24.48) * mm, "end": v(914.5, -39.73) * mm});
            skArc(sketch, "E124.9.0.12", {"start": v(876.91, 8.86) * mm, "mid": v(875, 0) * mm, "end": v(876.91, -8.86) * mm});
            skLineSegment(sketch, "E124.9.0.13", {"start": v(914.5, 39.73) * mm, "end": v(918.6, 24.48) * mm});
            skLineSegment(sketch, "E124.9.0.14", {"start": v(916.44, -42.25) * mm, "end": v(939, -42.25) * mm});
            skLineSegment(sketch, "E124.9.0.15", {"start": v(910.99, 42.25) * mm, "end": v(889.01, 42.25) * mm});
            skLineSegment(sketch, "E124.9.0.16", {"start": v(855, 39) * mm, "end": v(855, 11.88) * mm});
            skLineSegment(sketch, "E124.9.0.17", {"start": v(920.25, 7.4) * mm, "end": v(920.25, 19.25) * mm});
            skLineSegment(sketch, "E124.9.0.18", {"start": v(855, -11.88) * mm, "end": v(855, -39) * mm});
            skLineSegment(sketch, "E124.9.0.19", {"start": v(942.25, -39) * mm, "end": v(942.25, -16.44) * mm});
            skLineSegment(sketch, "E124.9.0.20", {"start": v(857.75, -16.44) * mm, "end": v(857.75, -39) * mm});
            skArc(sketch, "E124.9.0.21", {"start": v(861, 45) * mm, "mid": v(856.76, 43.24) * mm, "end": v(855, 39) * mm});
            skArc(sketch, "E124.9.0.22", {"start": v(923.09, -8.86) * mm, "mid": v(925, 0) * mm, "end": v(923.09, 8.86) * mm});
            skArc(sketch, "E124.9.0.23", {"start": v(908.86, 23.09) * mm, "mid": v(900, 25) * mm, "end": v(891.14, 23.09) * mm});
            skLineSegment(sketch, "E124.9.0.24", {"start": v(942.25, 16.44) * mm, "end": v(942.25, 39) * mm});
            skArc(sketch, "E124.9.0.25", {"start": v(855, -39) * mm, "mid": v(856.76, -43.24) * mm, "end": v(861, -45) * mm});
            skArc(sketch, "E124.9.0.26", {"start": v(920.3, -7.07) * mm, "mid": v(921.5, 0) * mm, "end": v(920.3, 7.07) * mm});
            skLineSegment(sketch, "E124.9.0.27", {"start": v(942.25, -10.99) * mm, "end": v(942.25, 10.99) * mm});
            skLineSegment(sketch, "E124.9.0.28", {"start": v(939.73, -14.5) * mm, "end": v(924.48, -18.6) * mm});
            skLineSegment(sketch, "E124.9.0.29", {"start": v(879.75, -7.4) * mm, "end": v(879.75, -19.25) * mm});
            skLineSegment(sketch, "E124.9.0.30", {"start": v(924.48, 18.6) * mm, "end": v(939.73, 14.5) * mm});
            skLineSegment(sketch, "E124.9.0.31", {"start": v(875.74, -15.8) * mm, "end": v(856.57, -10.67) * mm});
            skLineSegment(sketch, "E124.9.0.32", {"start": v(939, 42.25) * mm, "end": v(916.44, 42.25) * mm});
            skLineSegment(sketch, "E124.9.0.33", {"start": v(924.26, -15.8) * mm, "end": v(942.25, -10.99) * mm});
            skLineSegment(sketch, "E124.9.0.34", {"start": v(889.33, -43.43) * mm, "end": v(884.2, -24.26) * mm});
            skLineSegment(sketch, "E124.9.0.35", {"start": v(875.52, -18.6) * mm, "end": v(860.27, -14.5) * mm});
            skLineSegment(sketch, "E124.9.0.36", {"start": v(861, -42.25) * mm, "end": v(883.56, -42.25) * mm});
            skLineSegment(sketch, "E124.9.0.37", {"start": v(915.8, -24.26) * mm, "end": v(910.67, -43.43) * mm});
            skLineSegment(sketch, "E124.9.0.38", {"start": v(861, -45) * mm, "end": v(888.12, -45) * mm});
            skLineSegment(sketch, "E124.9.0.39", {"start": v(942.25, 10.99) * mm, "end": v(924.26, 15.8) * mm});
            skArc(sketch, "E124.9.0.40", {"start": v(879.7, 7.07) * mm, "mid": v(878.5, 0) * mm, "end": v(879.7, -7.07) * mm});
            skLineSegment(sketch, "E124.9.0.41", {"start": v(885.5, -39.73) * mm, "end": v(881.4, -24.48) * mm});
            skLineSegment(sketch, "E124.9.0.42", {"start": v(856.57, 10.67) * mm, "end": v(875.74, 15.8) * mm});
            skArc(sketch, "E124.9.0.43", {"start": v(945, 39) * mm, "mid": v(943.24, 43.24) * mm, "end": v(939, 45) * mm});
            skArc(sketch, "E124.9.0.44", {"start": v(891.14, -23.09) * mm, "mid": v(900, -25) * mm, "end": v(908.86, -23.09) * mm});
            skLineSegment(sketch, "E124.9.0.45", {"start": v(883.56, 42.25) * mm, "end": v(861, 42.25) * mm});
            skLineSegment(sketch, "E124.9.0.46", {"start": v(911.88, -45) * mm, "end": v(939, -45) * mm});
            skLineSegment(sketch, "E124.9.0.47", {"start": v(945, -39) * mm, "end": v(945, 39) * mm});
            skLineSegment(sketch, "E124.9.0.48", {"start": v(877, 14.84) * mm, "end": v(877, 9.27) * mm});
            skArc(sketch, "E124.9.0.49", {"start": v(857.75, 16.44) * mm, "mid": v(858.53, 14.85) * mm, "end": v(860.27, 14.5) * mm});
            skLineSegment(sketch, "E124.9.0.50", {"start": v(919.25, 20.25) * mm, "end": v(907.4, 20.25) * mm});
            skArc(sketch, "E124.9.0.51", {"start": v(914.84, 23) * mm, "mid": v(915.64, 23.4) * mm, "end": v(915.8, 24.26) * mm});
            skArc(sketch, "E124.9.0.52", {"start": v(884.2, 24.26) * mm, "mid": v(884.36, 23.4) * mm, "end": v(885.16, 23) * mm});
            skArc(sketch, "E124.9.0.53", {"start": v(856.57, -10.67) * mm, "mid": v(855.49, -10.89) * mm, "end": v(855, -11.88) * mm});
            skArc(sketch, "E124.9.0.54", {"start": v(877, 14.84) * mm, "mid": v(876.6, 15.64) * mm, "end": v(875.74, 15.8) * mm});
            skArc(sketch, "E124.9.0.55", {"start": v(885.5, 39.73) * mm, "mid": v(885.15, 41.47) * mm, "end": v(883.56, 42.25) * mm});
            skArc(sketch, "E124.9.0.56", {"start": v(939, -42.25) * mm, "mid": v(941.3, -41.3) * mm, "end": v(942.25, -39) * mm});
            skLineSegment(sketch, "E124.9.0.57", {"start": v(907.4, -20.25) * mm, "end": v(919.25, -20.25) * mm});
            skArc(sketch, "E124.9.0.58", {"start": v(861, 42.25) * mm, "mid": v(858.7, 41.3) * mm, "end": v(857.75, 39) * mm});
            skArc(sketch, "E124.9.0.59", {"start": v(883.56, -42.25) * mm, "mid": v(885.15, -41.47) * mm, "end": v(885.5, -39.73) * mm});
            skLineSegment(sketch, "E124.9.0.60", {"start": v(880.75, -20.25) * mm, "end": v(892.6, -20.25) * mm});
            skArc(sketch, "E124.9.0.61", {"start": v(923, -14.84) * mm, "mid": v(923.4, -15.64) * mm, "end": v(924.26, -15.8) * mm});
            skArc(sketch, "E124.9.0.62", {"start": v(942.25, -16.44) * mm, "mid": v(941.47, -14.85) * mm, "end": v(939.73, -14.5) * mm});
            skLineSegment(sketch, "E124.9.0.63", {"start": v(923, 14.84) * mm, "end": v(923, 9.27) * mm});
            skArc(sketch, "E124.9.0.64", {"start": v(860.27, -14.5) * mm, "mid": v(858.53, -14.85) * mm, "end": v(857.75, -16.44) * mm});
            skArc(sketch, "E124.9.0.65", {"start": v(916.44, 42.25) * mm, "mid": v(914.85, 41.47) * mm, "end": v(914.5, 39.73) * mm});
            skArc(sketch, "E124.9.0.66", {"start": v(910.67, -43.43) * mm, "mid": v(910.89, -44.51) * mm, "end": v(911.88, -45) * mm});
            skArc(sketch, "E124.9.0.67", {"start": v(918.6, 24.48) * mm, "mid": v(919.3, 23.41) * mm, "end": v(920.53, 23) * mm});
            skLineSegment(sketch, "E124.9.0.68", {"start": v(877, -9.27) * mm, "end": v(877, -14.84) * mm});
            skArc(sketch, "E124.9.0.69", {"start": v(875.74, -15.8) * mm, "mid": v(876.6, -15.64) * mm, "end": v(877, -14.84) * mm});
            skLineSegment(sketch, "E124.9.0.70", {"start": v(923, -9.27) * mm, "end": v(923, -14.84) * mm});
            skLineSegment(sketch, "E124.9.0.71", {"start": v(909.27, 23) * mm, "end": v(914.84, 23) * mm});
            skArc(sketch, "E124.9.0.72", {"start": v(855, 11.88) * mm, "mid": v(855.49, 10.89) * mm, "end": v(856.57, 10.67) * mm});
            skArc(sketch, "E124.9.0.73", {"start": v(939.73, 14.5) * mm, "mid": v(941.47, 14.85) * mm, "end": v(942.25, 16.44) * mm});
            skLineSegment(sketch, "E124.9.0.74", {"start": v(892.6, 20.25) * mm, "end": v(880.75, 20.25) * mm});
            skArc(sketch, "E124.9.0.75", {"start": v(914.5, -39.73) * mm, "mid": v(914.85, -41.47) * mm, "end": v(916.44, -42.25) * mm});
            skLineSegment(sketch, "E124.9.0.76", {"start": v(909.27, -23) * mm, "end": v(914.84, -23) * mm});
            skLineSegment(sketch, "E124.9.0.77", {"start": v(885.16, 23) * mm, "end": v(890.73, 23) * mm});
            skArc(sketch, "E124.9.0.78", {"start": v(920.25, 19.25) * mm, "mid": v(919.96, 19.96) * mm, "end": v(919.25, 20.25) * mm});
            skArc(sketch, "E124.9.0.79", {"start": v(942.25, 39) * mm, "mid": v(941.3, 41.3) * mm, "end": v(939, 42.25) * mm});
            skArc(sketch, "E124.9.0.80", {"start": v(920.53, -23) * mm, "mid": v(919.3, -23.41) * mm, "end": v(918.6, -24.48) * mm});
            skArc(sketch, "E124.9.0.81", {"start": v(879.47, 23) * mm, "mid": v(880.7, 23.41) * mm, "end": v(881.4, 24.48) * mm});
            skArc(sketch, "E124.9.0.82", {"start": v(915.8, -24.26) * mm, "mid": v(915.64, -23.4) * mm, "end": v(914.84, -23) * mm});
            skArc(sketch, "E124.9.0.83", {"start": v(885.16, -23) * mm, "mid": v(884.36, -23.4) * mm, "end": v(884.2, -24.26) * mm});
            skArc(sketch, "E124.9.0.84", {"start": v(919.25, -20.25) * mm, "mid": v(919.96, -19.96) * mm, "end": v(920.25, -19.25) * mm});
            skArc(sketch, "E124.9.0.85", {"start": v(879.75, -19.25) * mm, "mid": v(880.04, -19.96) * mm, "end": v(880.75, -20.25) * mm});
            skArc(sketch, "E124.9.0.86", {"start": v(880.75, 20.25) * mm, "mid": v(880.04, 19.96) * mm, "end": v(879.75, 19.25) * mm});
            skArc(sketch, "E124.9.0.87", {"start": v(888.12, -45) * mm, "mid": v(889.11, -44.51) * mm, "end": v(889.33, -43.43) * mm});
            skLineSegment(sketch, "E124.9.0.88", {"start": v(885.16, -23) * mm, "end": v(890.73, -23) * mm});
            skArc(sketch, "E124.9.0.89", {"start": v(881.4, -24.48) * mm, "mid": v(880.7, -23.41) * mm, "end": v(879.47, -23) * mm});
            skArc(sketch, "E124.9.0.90", {"start": v(857.75, -39) * mm, "mid": v(858.7, -41.3) * mm, "end": v(861, -42.25) * mm});
            skArc(sketch, "E124.9.0.91", {"start": v(924.26, 15.8) * mm, "mid": v(923.4, 15.64) * mm, "end": v(923, 14.84) * mm});
            skArc(sketch, "E124.9.0.92", {"start": v(923.09, -8.86) * mm, "mid": v(923.02, -9.06) * mm, "end": v(923, -9.27) * mm});
            skArc(sketch, "E124.9.0.93", {"start": v(877, -20.53) * mm, "mid": v(876.59, -19.3) * mm, "end": v(875.52, -18.6) * mm});
            skArc(sketch, "E124.9.0.94", {"start": v(877, -21) * mm, "mid": v(877.59, -22.41) * mm, "end": v(879, -23) * mm});
            skLineSegment(sketch, "E124.9.0.95", {"start": v(879, 23) * mm, "end": v(879.47, 23) * mm});
            skArc(sketch, "E124.9.0.96", {"start": v(908.86, 23.09) * mm, "mid": v(909.06, 23.02) * mm, "end": v(909.27, 23) * mm});
            skArc(sketch, "E124.9.0.97", {"start": v(923, 9.27) * mm, "mid": v(923.02, 9.06) * mm, "end": v(923.09, 8.86) * mm});
            skArc(sketch, "E124.9.0.98", {"start": v(920.25, 7.4) * mm, "mid": v(920.26, 7.23) * mm, "end": v(920.3, 7.07) * mm});
            skArc(sketch, "E124.9.0.99", {"start": v(879, 23) * mm, "mid": v(877.59, 22.41) * mm, "end": v(877, 21) * mm});
            skArc(sketch, "E124.9.0.100", {"start": v(879.75, -7.4) * mm, "mid": v(879.74, -7.23) * mm, "end": v(879.7, -7.07) * mm});
            skArc(sketch, "E124.9.0.101", {"start": v(876.91, 8.86) * mm, "mid": v(876.98, 9.06) * mm, "end": v(877, 9.27) * mm});
            skArc(sketch, "E124.9.0.102", {"start": v(892.6, 20.25) * mm, "mid": v(892.77, 20.26) * mm, "end": v(892.93, 20.3) * mm});
            skLineSegment(sketch, "E124.9.0.103", {"start": v(879.47, -23) * mm, "end": v(879, -23) * mm});
            skArc(sketch, "E124.9.0.104", {"start": v(920.3, -7.07) * mm, "mid": v(920.26, -7.23) * mm, "end": v(920.25, -7.4) * mm});
            skArc(sketch, "E124.9.0.105", {"start": v(879.7, 7.07) * mm, "mid": v(879.74, 7.23) * mm, "end": v(879.75, 7.4) * mm});
            skArc(sketch, "E124.9.0.106", {"start": v(890.73, 23) * mm, "mid": v(890.94, 23.02) * mm, "end": v(891.14, 23.09) * mm});
            skLineSegment(sketch, "E124.9.0.107", {"start": v(877, -21) * mm, "end": v(877, -20.53) * mm});
            skArc(sketch, "E124.9.0.108", {"start": v(875.52, 18.6) * mm, "mid": v(876.59, 19.3) * mm, "end": v(877, 20.53) * mm});
            skArc(sketch, "E124.9.0.109", {"start": v(877, -9.27) * mm, "mid": v(876.98, -9.06) * mm, "end": v(876.91, -8.86) * mm});
            skArc(sketch, "E124.9.0.110", {"start": v(907.07, 20.3) * mm, "mid": v(907.23, 20.26) * mm, "end": v(907.4, 20.25) * mm});
            skLineSegment(sketch, "E124.9.0.111", {"start": v(920.53, 23) * mm, "end": v(921, 23) * mm});
            skArc(sketch, "E124.9.0.112", {"start": v(924.48, -18.6) * mm, "mid": v(923.41, -19.3) * mm, "end": v(923, -20.53) * mm});
            skArc(sketch, "E124.9.0.113", {"start": v(907.4, -20.25) * mm, "mid": v(907.23, -20.26) * mm, "end": v(907.07, -20.3) * mm});
            skArc(sketch, "E124.9.0.114", {"start": v(921, -23) * mm, "mid": v(922.41, -22.41) * mm, "end": v(923, -21) * mm});
            skLineSegment(sketch, "E124.9.0.115", {"start": v(921, -23) * mm, "end": v(920.53, -23) * mm});
            skLineSegment(sketch, "E124.9.0.116", {"start": v(923, -20.53) * mm, "end": v(923, -21) * mm});
            skArc(sketch, "E124.9.0.117", {"start": v(909.27, -23) * mm, "mid": v(909.06, -23.02) * mm, "end": v(908.86, -23.09) * mm});
            skArc(sketch, "E124.9.0.118", {"start": v(891.14, -23.09) * mm, "mid": v(890.94, -23.02) * mm, "end": v(890.73, -23) * mm});
            skArc(sketch, "E124.9.0.119", {"start": v(923, 20.53) * mm, "mid": v(923.41, 19.3) * mm, "end": v(924.48, 18.6) * mm});
            skArc(sketch, "E124.9.0.120", {"start": v(892.93, -20.3) * mm, "mid": v(892.77, -20.26) * mm, "end": v(892.6, -20.25) * mm});
            skLineSegment(sketch, "E124.9.0.121", {"start": v(877, 20.53) * mm, "end": v(877, 21) * mm});
            skArc(sketch, "E124.9.0.122", {"start": v(923, 21) * mm, "mid": v(922.41, 22.41) * mm, "end": v(921, 23) * mm});
            skLineSegment(sketch, "E124.9.0.123", {"start": v(923, 21) * mm, "end": v(923, 20.53) * mm});
            skLineSegment(sketch, "E124.direction1", {"start": v(-39, -45) * mm, "end": v(61, -45) * mm, "construction": true});
            skSolve(sketch);
        }
        {
            var Q0;
            Q0=makeQuery(id+"F0.imprint","IMPRINT",FACE,{"disambiguationData":[TD([[makeQuery(id+"F0.imprint","IMPRINT",EDGE,{"derivedFrom":sQuery(id+"F0.wireOp",EDGE,"E0")}),-1.0]])]});
            extrude(context, id + "F1", {"entities" : qUnion([Q0]), "depth" : 1000 * mm, "offsetDistance" : 25 * mm});
        }
    });
